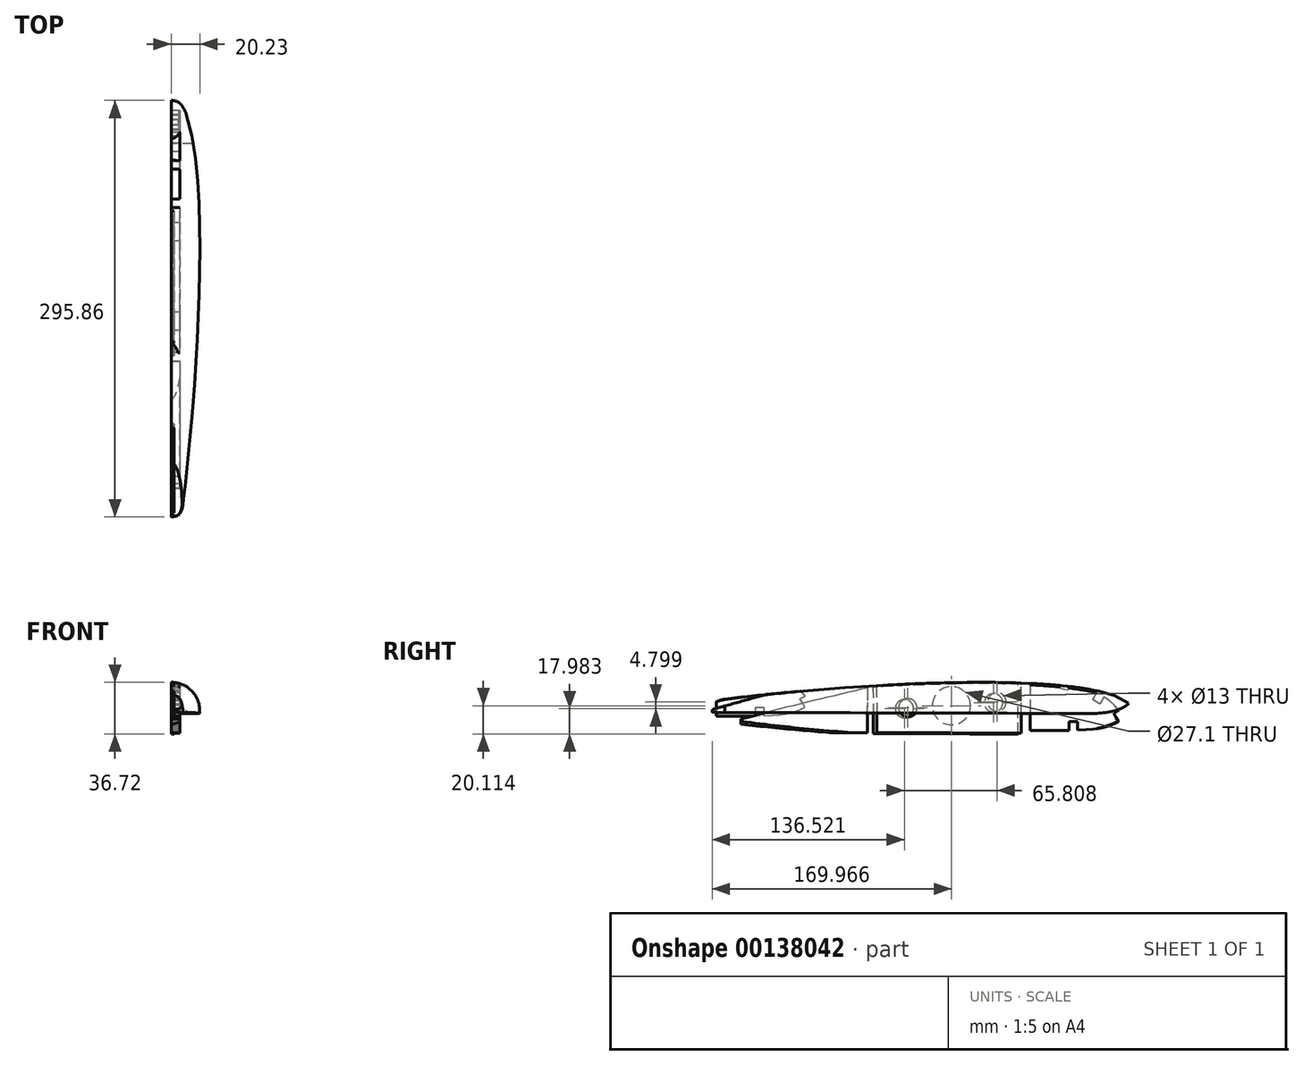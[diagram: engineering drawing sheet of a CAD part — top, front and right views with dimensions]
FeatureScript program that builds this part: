
annotation { "Feature Type Name" : "Feature", "Feature Type Description" : "" }
export const myFeature = defineFeature(function(context is Context, id is Id, definition is map)
    precondition{}
    {
        {
            var Q0;
            Q0=qCreatedBy(makeId("Right.planeOp"),FACE);
            var sketch = newSketch(context, id + "F0", { "sketchPlane" : qUnion([Q0])});
            skLineSegment(sketch, "E0", {"start": v(-158.36, 59.6) * mm, "end": v(-43.4, 59.28) * mm});
            skLineSegment(sketch, "E1", {"start": v(-43.4, 59.28) * mm, "end": v(-43.4, 68.43) * mm});
            skLineSegment(sketch, "E2", {"start": v(-43.4, 68.43) * mm, "end": v(-37.2, 68.43) * mm});
            skLineSegment(sketch, "E3", {"start": v(-37.2, 68.43) * mm, "end": v(-37.2, 59.28) * mm});
            skLineSegment(sketch, "E4", {"start": v(-37.2, 59.28) * mm, "end": v(65.82, 58.98) * mm});
            skLineSegment(sketch, "E5", {"start": v(65.82, 58.98) * mm, "end": v(65.82, 70.28) * mm});
            skLineSegment(sketch, "E6", {"start": v(65.82, 70.28) * mm, "end": v(72.02, 70.28) * mm});
            skLineSegment(sketch, "E7", {"start": v(72.02, 70.28) * mm, "end": v(72.02, 60.73) * mm});
            skLineSegment(sketch, "E8", {"start": v(72.02, 60.73) * mm, "end": v(99.85, 60.81) * mm});
            skLineSegment(sketch, "E9", {"start": v(99.85, 60.81) * mm, "end": v(99.85, 67.06) * mm});
            skLineSegment(sketch, "E10", {"start": v(99.85, 67.06) * mm, "end": v(105.7, 67.06) * mm});
            skLineSegment(sketch, "E11", {"start": v(105.7, 67.06) * mm, "end": v(105.7, 61.14) * mm});
            skLineSegment(sketch, "E12", {"start": v(105.7, 61.14) * mm, "end": v(111.6, 61.4) * mm});
            skLineSegment(sketch, "E13", {"start": v(111.6, 61.4) * mm, "end": v(116.68, 61.82) * mm});
            skLineSegment(sketch, "E14", {"start": v(116.68, 61.82) * mm, "end": v(121.05, 62.42) * mm});
            skLineSegment(sketch, "E15", {"start": v(121.05, 62.42) * mm, "end": v(124.86, 63.23) * mm});
            skLineSegment(sketch, "E16", {"start": v(124.86, 63.23) * mm, "end": v(128.31, 64.27) * mm});
            skLineSegment(sketch, "E17", {"start": v(128.31, 64.27) * mm, "end": v(131.85, 65.67) * mm});
            skLineSegment(sketch, "E18", {"start": v(131.85, 65.67) * mm, "end": v(134.32, 66.87) * mm});
            skLineSegment(sketch, "E19", {"start": v(134.32, 66.87) * mm, "end": v(130.67, 73.42) * mm});
            skLineSegment(sketch, "E20", {"start": v(130.67, 73.42) * mm, "end": v(134.6, 75.6) * mm});
            skLineSegment(sketch, "E21", {"start": v(134.6, 75.6) * mm, "end": v(132.03, 78.53) * mm});
            skLineSegment(sketch, "E22", {"start": v(132.03, 78.53) * mm, "end": v(128.46, 81.7) * mm});
            skLineSegment(sketch, "E23", {"start": v(128.46, 81.7) * mm, "end": v(124.52, 84.4) * mm});
            skLineSegment(sketch, "E24", {"start": v(124.52, 84.4) * mm, "end": v(121.47, 79.12) * mm});
            skLineSegment(sketch, "E25", {"start": v(121.47, 79.12) * mm, "end": v(116.13, 82.2) * mm});
            skLineSegment(sketch, "E26", {"start": v(116.13, 82.2) * mm, "end": v(119.34, 87.78) * mm});
            skLineSegment(sketch, "E27", {"start": v(119.34, 87.78) * mm, "end": v(115.72, 89.55) * mm});
            skLineSegment(sketch, "E28", {"start": v(115.72, 89.55) * mm, "end": v(112.05, 91.25) * mm});
            skLineSegment(sketch, "E29", {"start": v(112.05, 91.25) * mm, "end": v(108.3, 92.8) * mm});
            skLineSegment(sketch, "E30", {"start": v(108.3, 92.8) * mm, "end": v(104.53, 94.12) * mm});
            skLineSegment(sketch, "E31", {"start": v(104.53, 94.12) * mm, "end": v(100.47, 95.16) * mm});
            skLineSegment(sketch, "E32", {"start": v(100.47, 95.16) * mm, "end": v(98.76, 89.3) * mm});
            skLineSegment(sketch, "E33", {"start": v(98.76, 89.3) * mm, "end": v(92.83, 91.04) * mm});
            skLineSegment(sketch, "E34", {"start": v(92.83, 91.04) * mm, "end": v(94.63, 97.2) * mm});
            skLineSegment(sketch, "E35", {"start": v(94.63, 97.2) * mm, "end": v(90.15, 98.07) * mm});
            skLineSegment(sketch, "E36", {"start": v(90.15, 98.07) * mm, "end": v(85.63, 98.85) * mm});
            skLineSegment(sketch, "E37", {"start": v(85.63, 98.85) * mm, "end": v(80.98, 99.54) * mm});
            skLineSegment(sketch, "E38", {"start": v(80.98, 99.54) * mm, "end": v(76.61, 100.13) * mm});
            skLineSegment(sketch, "E39", {"start": v(76.61, 100.13) * mm, "end": v(72.02, 100.6) * mm});
            skLineSegment(sketch, "E40", {"start": v(72.02, 100.6) * mm, "end": v(72.02, 90.28) * mm});
            skLineSegment(sketch, "E41", {"start": v(72.02, 90.28) * mm, "end": v(65.82, 90.28) * mm});
            skLineSegment(sketch, "E42", {"start": v(65.82, 90.28) * mm, "end": v(65.82, 102.3) * mm});
            skLineSegment(sketch, "E43", {"start": v(65.82, 102.3) * mm, "end": v(59.19, 102.27) * mm});
            skLineSegment(sketch, "E44", {"start": v(59.19, 102.27) * mm, "end": v(52.86, 102.17) * mm});
            skLineSegment(sketch, "E45", {"start": v(52.86, 102.17) * mm, "end": v(46.82, 102) * mm});
            skLineSegment(sketch, "E46", {"start": v(46.82, 102) * mm, "end": v(41.06, 101.78) * mm});
            skLineSegment(sketch, "E47", {"start": v(41.06, 101.78) * mm, "end": v(35.53, 101.5) * mm});
            skLineSegment(sketch, "E48", {"start": v(35.53, 101.5) * mm, "end": v(30.24, 101.17) * mm});
            skLineSegment(sketch, "E49", {"start": v(30.24, 101.17) * mm, "end": v(25.14, 100.8) * mm});
            skLineSegment(sketch, "E50", {"start": v(25.14, 100.8) * mm, "end": v(20.23, 100.36) * mm});
            skLineSegment(sketch, "E51", {"start": v(20.23, 100.36) * mm, "end": v(15.48, 99.9) * mm});
            skLineSegment(sketch, "E52", {"start": v(15.48, 99.9) * mm, "end": v(10.86, 99.38) * mm});
            skLineSegment(sketch, "E53", {"start": v(10.86, 99.38) * mm, "end": v(6.36, 98.83) * mm});
            skLineSegment(sketch, "E54", {"start": v(6.36, 98.83) * mm, "end": v(1.95, 98.25) * mm});
            skLineSegment(sketch, "E55", {"start": v(1.95, 98.25) * mm, "end": v(-2.38, 97.64) * mm});
            skLineSegment(sketch, "E56", {"start": v(-2.38, 97.64) * mm, "end": v(-6.67, 97) * mm});
            skLineSegment(sketch, "E57", {"start": v(-6.67, 97) * mm, "end": v(-10.93, 96.35) * mm});
            skLineSegment(sketch, "E58", {"start": v(-10.93, 96.35) * mm, "end": v(-15.18, 95.67) * mm});
            skLineSegment(sketch, "E59", {"start": v(-15.18, 95.67) * mm, "end": v(-19.45, 94.98) * mm});
            skLineSegment(sketch, "E60", {"start": v(-19.45, 94.98) * mm, "end": v(-23.75, 94.27) * mm});
            skLineSegment(sketch, "E61", {"start": v(-23.75, 94.27) * mm, "end": v(-28.12, 93.55) * mm});
            skLineSegment(sketch, "E62", {"start": v(-28.12, 93.55) * mm, "end": v(-32.66, 92.83) * mm});
            skLineSegment(sketch, "E63", {"start": v(-32.66, 92.83) * mm, "end": v(-37.2, 92.1) * mm});
            skLineSegment(sketch, "E64", {"start": v(-37.2, 92.1) * mm, "end": v(-37.2, 81.43) * mm});
            skLineSegment(sketch, "E65", {"start": v(-37.2, 81.43) * mm, "end": v(-43.4, 81.43) * mm});
            skLineSegment(sketch, "E66", {"start": v(-43.4, 81.43) * mm, "end": v(-43.4, 91.03) * mm});
            skLineSegment(sketch, "E67", {"start": v(-43.4, 91.03) * mm, "end": v(-48.14, 89.92) * mm});
            skLineSegment(sketch, "E68", {"start": v(-48.14, 89.92) * mm, "end": v(-52.97, 88.81) * mm});
            skLineSegment(sketch, "E69", {"start": v(-52.97, 88.81) * mm, "end": v(-57.8, 87.7) * mm});
            skLineSegment(sketch, "E70", {"start": v(-57.8, 87.7) * mm, "end": v(-62.63, 86.58) * mm});
            skLineSegment(sketch, "E71", {"start": v(-62.63, 86.58) * mm, "end": v(-67.45, 85.45) * mm});
            skLineSegment(sketch, "E72", {"start": v(-67.45, 85.45) * mm, "end": v(-72.27, 84.3) * mm});
            skLineSegment(sketch, "E73", {"start": v(-72.27, 84.3) * mm, "end": v(-77.1, 83.16) * mm});
            skLineSegment(sketch, "E74", {"start": v(-77.1, 83.16) * mm, "end": v(-81.9, 82) * mm});
            skLineSegment(sketch, "E75", {"start": v(-81.9, 82) * mm, "end": v(-86.72, 80.84) * mm});
            skLineSegment(sketch, "E76", {"start": v(-86.72, 80.84) * mm, "end": v(-91.53, 79.66) * mm});
            skLineSegment(sketch, "E77", {"start": v(-91.53, 79.66) * mm, "end": v(-96.34, 78.48) * mm});
            skLineSegment(sketch, "E78", {"start": v(-96.34, 78.48) * mm, "end": v(-101.14, 77.28) * mm});
            skLineSegment(sketch, "E79", {"start": v(-101.14, 77.28) * mm, "end": v(-105.94, 76.07) * mm});
            skLineSegment(sketch, "E80", {"start": v(-105.94, 76.07) * mm, "end": v(-110.73, 74.85) * mm});
            skLineSegment(sketch, "E81", {"start": v(-110.73, 74.85) * mm, "end": v(-115.52, 73.61) * mm});
            skLineSegment(sketch, "E82", {"start": v(-115.52, 73.61) * mm, "end": v(-120.3, 72.36) * mm});
            skLineSegment(sketch, "E83", {"start": v(-120.3, 72.36) * mm, "end": v(-125.08, 71.1) * mm});
            skLineSegment(sketch, "E84", {"start": v(-125.08, 71.1) * mm, "end": v(-129.85, 69.83) * mm});
            skLineSegment(sketch, "E85", {"start": v(-129.85, 69.83) * mm, "end": v(-134.62, 68.54) * mm});
            skLineSegment(sketch, "E86", {"start": v(-134.62, 68.54) * mm, "end": v(-139.38, 67.23) * mm});
            skLineSegment(sketch, "E87", {"start": v(-139.38, 67.23) * mm, "end": v(-144.14, 65.9) * mm});
            skLineSegment(sketch, "E88", {"start": v(-144.14, 65.9) * mm, "end": v(-148.88, 64.57) * mm});
            skLineSegment(sketch, "E89", {"start": v(-148.88, 64.57) * mm, "end": v(-153.62, 63.21) * mm});
            skLineSegment(sketch, "E90", {"start": v(-153.62, 63.21) * mm, "end": v(-158.36, 61.84) * mm});
            skLineSegment(sketch, "E91", {"start": v(-158.36, 61.84) * mm, "end": v(-158.36, 59.6) * mm});
            skCircle(sketch, "E92", {"center": v(18.63, 79.1) * mm, "radius": 13.55 * mm});
            skPoint(sketch, "E93.end.orphan", {"position": v(5.17, 79.1) * mm});
            skPoint(sketch, "E94.end.orphan", {"position": v(32.08, 79.1) * mm});
            skCircle(sketch, "E95", {"center": v(48.53, 81.13) * mm, "radius": 6.5 * mm});
            skPoint(sketch, "E96.start.orphan", {"position": v(42.17, 81.13) * mm});
            skPoint(sketch, "E97.end.orphan", {"position": v(48.53, 87.5) * mm});
            skCircle(sketch, "E98", {"center": v(-14.82, 76.96) * mm, "radius": 6.5 * mm});
            skPoint(sketch, "E99.end.orphan", {"position": v(-14.82, 83.33) * mm});
            skPoint(sketch, "E100.end.orphan", {"position": v(-21.19, 76.96) * mm});
            skCircle(sketch, "E101", {"center": v(117.36, 70.19) * mm, "radius": 3 * mm});
            skPoint(sketch, "E102.end.orphan", {"position": v(117.36, 73.15) * mm});
            skPoint(sketch, "E103.end.orphan", {"position": v(114.4, 70.19) * mm});
            skCircle(sketch, "E104", {"center": v(-96.87, 68.9) * mm, "radius": 3 * mm});
            skPoint(sketch, "E105.end.orphan", {"position": v(-96.87, 71.86) * mm});
            skPoint(sketch, "E106.end.orphan", {"position": v(-99.84, 68.9) * mm});
            skSolve(sketch);
        }
        {
            var Q0;
            Q0=makeQuery(id+"F0.imprint","IMPRINT",FACE,{"disambiguationData":[TD([[makeQuery(id+"F0.imprint","IMPRINT",EDGE,{"derivedFrom":sQuery(id+"F0.wireOp",EDGE,"E0")}),1.0]])]});
            extrude(context, id + "F1", {"entities" : qUnion([Q0]), "depth" : 6 * mm});
        }
        {
            var Q0;
            Q0=qCreatedBy(makeId("Right.planeOp"),FACE);
            var sketch = newSketch(context, id + "F2", { "sketchPlane" : qUnion([Q0])});
            skLineSegment(sketch, "E107", {"start": v(-44.93, 16.54) * mm, "end": v(-44.6, -16.3) * mm});
            skLineSegment(sketch, "E108", {"start": v(-44.6, -16.3) * mm, "end": v(-39.7, -16.3) * mm});
            skLineSegment(sketch, "E109", {"start": v(-39.7, -16.3) * mm, "end": v(-34.82, -16.32) * mm});
            skLineSegment(sketch, "E110", {"start": v(-34.82, -16.32) * mm, "end": v(-29.94, -16.33) * mm});
            skLineSegment(sketch, "E111", {"start": v(-29.94, -16.33) * mm, "end": v(-25.05, -16.35) * mm});
            skLineSegment(sketch, "E112", {"start": v(-25.05, -16.35) * mm, "end": v(-20.17, -16.36) * mm});
            skLineSegment(sketch, "E113", {"start": v(-20.17, -16.36) * mm, "end": v(-15.28, -16.38) * mm});
            skLineSegment(sketch, "E114", {"start": v(-15.28, -16.38) * mm, "end": v(-10.4, -16.4) * mm});
            skLineSegment(sketch, "E115", {"start": v(-10.4, -16.4) * mm, "end": v(-5.5, -16.4) * mm});
            skLineSegment(sketch, "E116", {"start": v(-5.5, -16.4) * mm, "end": v(-0.62, -16.42) * mm});
            skLineSegment(sketch, "E117", {"start": v(-0.62, -16.42) * mm, "end": v(4.26, -16.43) * mm});
            skLineSegment(sketch, "E118", {"start": v(4.26, -16.43) * mm, "end": v(9.15, -16.45) * mm});
            skLineSegment(sketch, "E119", {"start": v(9.15, -16.45) * mm, "end": v(14.03, -16.46) * mm});
            skLineSegment(sketch, "E120", {"start": v(14.03, -16.46) * mm, "end": v(18.92, -16.48) * mm});
            skLineSegment(sketch, "E121", {"start": v(18.92, -16.48) * mm, "end": v(23.8, -16.5) * mm});
            skLineSegment(sketch, "E122", {"start": v(23.8, -16.5) * mm, "end": v(28.69, -16.5) * mm});
            skLineSegment(sketch, "E123", {"start": v(28.69, -16.5) * mm, "end": v(33.57, -16.52) * mm});
            skLineSegment(sketch, "E124", {"start": v(33.57, -16.52) * mm, "end": v(38.46, -16.53) * mm});
            skLineSegment(sketch, "E125", {"start": v(38.46, -16.53) * mm, "end": v(43.35, -16.55) * mm});
            skLineSegment(sketch, "E126", {"start": v(43.35, -16.55) * mm, "end": v(48.23, -16.56) * mm});
            skLineSegment(sketch, "E127", {"start": v(48.23, -16.56) * mm, "end": v(53.12, -16.58) * mm});
            skLineSegment(sketch, "E128", {"start": v(53.12, -16.58) * mm, "end": v(58, -16.6) * mm});
            skLineSegment(sketch, "E129", {"start": v(58, -16.6) * mm, "end": v(58, 26.73) * mm});
            skLineSegment(sketch, "E130", {"start": v(51.37, 26.7) * mm, "end": v(45.04, 26.6) * mm});
            skLineSegment(sketch, "E131", {"start": v(45.04, 26.6) * mm, "end": v(39, 26.43) * mm});
            skLineSegment(sketch, "E132", {"start": v(39, 26.43) * mm, "end": v(33.23, 26.21) * mm});
            skLineSegment(sketch, "E133", {"start": v(33.23, 26.21) * mm, "end": v(27.71, 25.93) * mm});
            skLineSegment(sketch, "E134", {"start": v(27.71, 25.93) * mm, "end": v(22.42, 25.6) * mm});
            skLineSegment(sketch, "E135", {"start": v(22.42, 25.6) * mm, "end": v(17.32, 25.22) * mm});
            skLineSegment(sketch, "E136", {"start": v(17.32, 25.22) * mm, "end": v(12.4, 24.8) * mm});
            skLineSegment(sketch, "E137", {"start": v(12.4, 24.8) * mm, "end": v(7.65, 24.32) * mm});
            skLineSegment(sketch, "E138", {"start": v(7.65, 24.32) * mm, "end": v(3.04, 23.8) * mm});
            skLineSegment(sketch, "E139", {"start": v(3.04, 23.8) * mm, "end": v(-1.46, 23.26) * mm});
            skLineSegment(sketch, "E140", {"start": v(-1.46, 23.26) * mm, "end": v(-5.87, 22.68) * mm});
            skLineSegment(sketch, "E141", {"start": v(-5.87, 22.68) * mm, "end": v(-10.2, 22.07) * mm});
            skLineSegment(sketch, "E142", {"start": v(-10.2, 22.07) * mm, "end": v(-14.5, 21.44) * mm});
            skLineSegment(sketch, "E143", {"start": v(-14.5, 21.44) * mm, "end": v(-18.75, 20.78) * mm});
            skLineSegment(sketch, "E144", {"start": v(-18.75, 20.78) * mm, "end": v(-23, 20.1) * mm});
            skLineSegment(sketch, "E145", {"start": v(-23, 20.1) * mm, "end": v(-27.27, 19.4) * mm});
            skLineSegment(sketch, "E146", {"start": v(-27.27, 19.4) * mm, "end": v(-31.57, 18.7) * mm});
            skLineSegment(sketch, "E147", {"start": v(-31.57, 18.7) * mm, "end": v(-35.94, 17.98) * mm});
            skLineSegment(sketch, "E148", {"start": v(-35.94, 17.98) * mm, "end": v(-40.38, 17.26) * mm});
            skLineSegment(sketch, "E149", {"start": v(-40.38, 17.26) * mm, "end": v(-44.93, 16.54) * mm});
            skCircle(sketch, "E150", {"center": v(10.8, 3.52) * mm, "radius": 13.55 * mm});
            skCircle(sketch, "E151", {"center": v(40.71, 5.56) * mm, "radius": 6.5 * mm});
            skCircle(sketch, "E152", {"center": v(-22.64, 1.4) * mm, "radius": 6.5 * mm});
            skLineSegment(sketch, "E153", {"start": v(51.37, 26.7) * mm, "end": v(58, 26.73) * mm});
            skLineSegment(sketch, "E154", {"start": v(-271.5, -5.35) * mm, "end": v(-271.4, 26.4) * mm});
            skLineSegment(sketch, "E155", {"start": v(-156.16, 35.97) * mm, "end": v(-156.16, -3.9) * mm});
            skLineSegment(sketch, "E156", {"start": v(-156.16, -3.9) * mm, "end": v(-151.52, -3.88) * mm});
            skLineSegment(sketch, "E157", {"start": v(-151.52, -3.88) * mm, "end": v(-146.89, -3.87) * mm});
            skLineSegment(sketch, "E158", {"start": v(-146.89, -3.87) * mm, "end": v(-142.25, -3.85) * mm});
            skLineSegment(sketch, "E159", {"start": v(-142.25, -3.85) * mm, "end": v(-137.61, -3.84) * mm});
            skLineSegment(sketch, "E160", {"start": v(-137.61, -3.84) * mm, "end": v(-132.97, -3.83) * mm});
            skLineSegment(sketch, "E161", {"start": v(-132.97, -3.83) * mm, "end": v(-128.34, -3.81) * mm});
            skLineSegment(sketch, "E162", {"start": v(-128.34, -3.81) * mm, "end": v(-128.34, -0.7) * mm});
            skLineSegment(sketch, "E163", {"start": v(-128.34, -0.7) * mm, "end": v(-128.34, 2.43) * mm});
            skLineSegment(sketch, "E164", {"start": v(-128.34, 2.43) * mm, "end": v(-125.42, 2.43) * mm});
            skLineSegment(sketch, "E165", {"start": v(-125.42, 2.43) * mm, "end": v(-122.5, 2.43) * mm});
            skLineSegment(sketch, "E166", {"start": v(-122.5, 2.43) * mm, "end": v(-122.5, -0.53) * mm});
            skLineSegment(sketch, "E167", {"start": v(-122.5, -0.53) * mm, "end": v(-122.5, -3.49) * mm});
            skLineSegment(sketch, "E168", {"start": v(-122.5, -3.49) * mm, "end": v(-116.5, -3.23) * mm});
            skLineSegment(sketch, "E169", {"start": v(-116.5, -3.23) * mm, "end": v(-111.4, -2.8) * mm});
            skLineSegment(sketch, "E170", {"start": v(-111.4, -2.8) * mm, "end": v(-107.04, -2.2) * mm});
            skLineSegment(sketch, "E171", {"start": v(-107.04, -2.2) * mm, "end": v(-103.22, -1.4) * mm});
            skLineSegment(sketch, "E172", {"start": v(-103.22, -1.4) * mm, "end": v(-99.77, -0.36) * mm});
            skLineSegment(sketch, "E173", {"start": v(-99.77, -0.36) * mm, "end": v(-96.52, 0.94) * mm});
            skLineSegment(sketch, "E174", {"start": v(-96.52, 0.94) * mm, "end": v(-93.27, 2.52) * mm});
            skLineSegment(sketch, "E175", {"start": v(-93.27, 2.52) * mm, "end": v(-94.98, 5.5) * mm});
            skLineSegment(sketch, "E176", {"start": v(-94.98, 5.5) * mm, "end": v(-96.69, 8.47) * mm});
            skLineSegment(sketch, "E177", {"start": v(-96.69, 8.47) * mm, "end": v(-93.06, 10.5) * mm});
            skLineSegment(sketch, "E178", {"start": v(-93.06, 10.5) * mm, "end": v(-96.06, 13.9) * mm});
            skLineSegment(sketch, "E179", {"start": v(-96.06, 13.9) * mm, "end": v(-99.62, 17.07) * mm});
            skLineSegment(sketch, "E180", {"start": v(-99.62, 17.07) * mm, "end": v(-103.65, 20.07) * mm});
            skLineSegment(sketch, "E181", {"start": v(-103.65, 20.07) * mm, "end": v(-105.04, 17.44) * mm});
            skLineSegment(sketch, "E182", {"start": v(-105.04, 17.44) * mm, "end": v(-106.43, 14.82) * mm});
            skLineSegment(sketch, "E183", {"start": v(-106.43, 14.82) * mm, "end": v(-109.05, 16.44) * mm});
            skLineSegment(sketch, "E184", {"start": v(-109.05, 16.44) * mm, "end": v(-111.68, 18.06) * mm});
            skLineSegment(sketch, "E185", {"start": v(-111.68, 18.06) * mm, "end": v(-110.21, 20.6) * mm});
            skLineSegment(sketch, "E186", {"start": v(-110.21, 20.6) * mm, "end": v(-108.74, 23.16) * mm});
            skLineSegment(sketch, "E187", {"start": v(-108.74, 23.16) * mm, "end": v(-112.37, 24.92) * mm});
            skLineSegment(sketch, "E188", {"start": v(-112.37, 24.92) * mm, "end": v(-116.04, 26.62) * mm});
            skLineSegment(sketch, "E189", {"start": v(-116.04, 26.62) * mm, "end": v(-119.8, 28.18) * mm});
            skLineSegment(sketch, "E190", {"start": v(-119.8, 28.18) * mm, "end": v(-123.68, 29.52) * mm});
            skLineSegment(sketch, "E191", {"start": v(-123.68, 29.52) * mm, "end": v(-127.74, 30.57) * mm});
            skLineSegment(sketch, "E192", {"start": v(-127.74, 30.57) * mm, "end": v(-128.5, 27.71) * mm});
            skLineSegment(sketch, "E193", {"start": v(-128.5, 27.71) * mm, "end": v(-129.28, 24.85) * mm});
            skLineSegment(sketch, "E194", {"start": v(-129.28, 24.85) * mm, "end": v(-132.3, 25.55) * mm});
            skLineSegment(sketch, "E195", {"start": v(-132.3, 25.55) * mm, "end": v(-135.3, 26.24) * mm});
            skLineSegment(sketch, "E196", {"start": v(-135.3, 26.24) * mm, "end": v(-134.38, 29.4) * mm});
            skLineSegment(sketch, "E197", {"start": v(-134.38, 29.4) * mm, "end": v(-133.45, 32.58) * mm});
            skLineSegment(sketch, "E198", {"start": v(-133.45, 32.58) * mm, "end": v(-137.94, 33.44) * mm});
            skLineSegment(sketch, "E199", {"start": v(-137.94, 33.44) * mm, "end": v(-142.46, 34.22) * mm});
            skLineSegment(sketch, "E200", {"start": v(-142.46, 34.22) * mm, "end": v(-147, 34.91) * mm});
            skLineSegment(sketch, "E201", {"start": v(-147, 34.91) * mm, "end": v(-151.57, 35.5) * mm});
            skLineSegment(sketch, "E202", {"start": v(-151.57, 35.5) * mm, "end": v(-156.16, 35.97) * mm});
            skLineSegment(sketch, "E203", {"start": v(-271.4, 26.4) * mm, "end": v(-276.23, 25.3) * mm});
            skLineSegment(sketch, "E204", {"start": v(-276.23, 25.3) * mm, "end": v(-281.06, 24.19) * mm});
            skLineSegment(sketch, "E205", {"start": v(-281.06, 24.19) * mm, "end": v(-285.89, 23.07) * mm});
            skLineSegment(sketch, "E206", {"start": v(-285.89, 23.07) * mm, "end": v(-290.71, 21.95) * mm});
            skLineSegment(sketch, "E207", {"start": v(-290.71, 21.95) * mm, "end": v(-295.54, 20.82) * mm});
            skLineSegment(sketch, "E208", {"start": v(-295.54, 20.82) * mm, "end": v(-300.36, 19.68) * mm});
            skLineSegment(sketch, "E209", {"start": v(-300.36, 19.68) * mm, "end": v(-305.18, 18.53) * mm});
            skLineSegment(sketch, "E210", {"start": v(-305.18, 18.53) * mm, "end": v(-310, 17.38) * mm});
            skLineSegment(sketch, "E211", {"start": v(-310, 17.38) * mm, "end": v(-314.8, 16.21) * mm});
            skLineSegment(sketch, "E212", {"start": v(-314.8, 16.21) * mm, "end": v(-319.62, 15.03) * mm});
            skLineSegment(sketch, "E213", {"start": v(-319.62, 15.03) * mm, "end": v(-324.43, 13.85) * mm});
            skLineSegment(sketch, "E214", {"start": v(-324.43, 13.85) * mm, "end": v(-329.23, 12.65) * mm});
            skLineSegment(sketch, "E215", {"start": v(-329.23, 12.65) * mm, "end": v(-334.03, 11.44) * mm});
            skLineSegment(sketch, "E216", {"start": v(-334.03, 11.44) * mm, "end": v(-338.82, 10.22) * mm});
            skLineSegment(sketch, "E217", {"start": v(-338.82, 10.22) * mm, "end": v(-343.6, 8.98) * mm});
            skLineSegment(sketch, "E218", {"start": v(-343.6, 8.98) * mm, "end": v(-348.4, 7.74) * mm});
            skLineSegment(sketch, "E219", {"start": v(-348.4, 7.74) * mm, "end": v(-353.17, 6.47) * mm});
            skLineSegment(sketch, "E220", {"start": v(-353.17, 6.47) * mm, "end": v(-357.94, 5.2) * mm});
            skLineSegment(sketch, "E221", {"start": v(-271.5, -5.35) * mm, "end": v(-361.14, -5.08) * mm});
            skLineSegment(sketch, "E222", {"start": v(-361.14, -5.08) * mm, "end": v(-361.14, 4.33) * mm});
            skLineSegment(sketch, "E223", {"start": v(-361.14, 4.33) * mm, "end": v(-357.94, 5.2) * mm});
            skSolve(sketch);
        }
        {
            var Q0;
            Q0=qCreatedBy(makeId("Right.planeOp"),FACE);
            var sketch = newSketch(context, id + "F3", { "sketchPlane" : qUnion([Q0])});
            skLineSegment(sketch, "E224", {"start": v(-48.77, -15.66) * mm, "end": v(-48.68, 16.08) * mm});
            skLineSegment(sketch, "E225", {"start": v(-42.47, 17.17) * mm, "end": v(-42.14, -15.66) * mm});
            skLineSegment(sketch, "E226", {"start": v(-42.14, -15.66) * mm, "end": v(-37.25, -15.68) * mm});
            skLineSegment(sketch, "E227", {"start": v(-37.25, -15.68) * mm, "end": v(-32.36, -15.7) * mm});
            skLineSegment(sketch, "E228", {"start": v(-32.36, -15.7) * mm, "end": v(-27.48, -15.7) * mm});
            skLineSegment(sketch, "E229", {"start": v(-27.48, -15.7) * mm, "end": v(-22.6, -15.72) * mm});
            skLineSegment(sketch, "E230", {"start": v(-22.6, -15.72) * mm, "end": v(-17.7, -15.73) * mm});
            skLineSegment(sketch, "E231", {"start": v(-17.7, -15.73) * mm, "end": v(-12.82, -15.75) * mm});
            skLineSegment(sketch, "E232", {"start": v(-12.82, -15.75) * mm, "end": v(-7.94, -15.76) * mm});
            skLineSegment(sketch, "E233", {"start": v(-7.94, -15.76) * mm, "end": v(-3.05, -15.78) * mm});
            skLineSegment(sketch, "E234", {"start": v(-3.05, -15.78) * mm, "end": v(1.83, -15.8) * mm});
            skLineSegment(sketch, "E235", {"start": v(1.83, -15.8) * mm, "end": v(6.72, -15.8) * mm});
            skLineSegment(sketch, "E236", {"start": v(6.72, -15.8) * mm, "end": v(11.6, -15.82) * mm});
            skLineSegment(sketch, "E237", {"start": v(11.6, -15.82) * mm, "end": v(16.5, -15.83) * mm});
            skLineSegment(sketch, "E238", {"start": v(16.5, -15.83) * mm, "end": v(21.38, -15.85) * mm});
            skLineSegment(sketch, "E239", {"start": v(21.38, -15.85) * mm, "end": v(26.26, -15.86) * mm});
            skLineSegment(sketch, "E240", {"start": v(26.26, -15.86) * mm, "end": v(31.15, -15.88) * mm});
            skLineSegment(sketch, "E241", {"start": v(31.15, -15.88) * mm, "end": v(36.03, -15.9) * mm});
            skLineSegment(sketch, "E242", {"start": v(36.03, -15.9) * mm, "end": v(40.92, -15.9) * mm});
            skLineSegment(sketch, "E243", {"start": v(40.92, -15.9) * mm, "end": v(45.8, -15.92) * mm});
            skLineSegment(sketch, "E244", {"start": v(45.8, -15.92) * mm, "end": v(50.69, -15.93) * mm});
            skLineSegment(sketch, "E245", {"start": v(50.69, -15.93) * mm, "end": v(55.57, -15.95) * mm});
            skLineSegment(sketch, "E246", {"start": v(55.57, -15.95) * mm, "end": v(60.46, -15.96) * mm});
            skLineSegment(sketch, "E247", {"start": v(60.46, -15.96) * mm, "end": v(60.46, 27.36) * mm});
            skLineSegment(sketch, "E248", {"start": v(66.56, 25.66) * mm, "end": v(66.56, -14.2) * mm});
            skLineSegment(sketch, "E249", {"start": v(66.56, -14.2) * mm, "end": v(71.2, -14.2) * mm});
            skLineSegment(sketch, "E250", {"start": v(71.2, -14.2) * mm, "end": v(75.84, -14.18) * mm});
            skLineSegment(sketch, "E251", {"start": v(75.84, -14.18) * mm, "end": v(80.47, -14.17) * mm});
            skLineSegment(sketch, "E252", {"start": v(80.47, -14.17) * mm, "end": v(85.11, -14.15) * mm});
            skLineSegment(sketch, "E253", {"start": v(85.11, -14.15) * mm, "end": v(89.75, -14.14) * mm});
            skLineSegment(sketch, "E254", {"start": v(89.75, -14.14) * mm, "end": v(94.39, -14.13) * mm});
            skLineSegment(sketch, "E255", {"start": v(94.39, -14.13) * mm, "end": v(94.39, -11) * mm});
            skLineSegment(sketch, "E256", {"start": v(94.39, -11) * mm, "end": v(94.39, -7.88) * mm});
            skLineSegment(sketch, "E257", {"start": v(94.39, -7.88) * mm, "end": v(97.3, -7.88) * mm});
            skLineSegment(sketch, "E258", {"start": v(97.3, -7.88) * mm, "end": v(100.23, -7.88) * mm});
            skLineSegment(sketch, "E259", {"start": v(100.23, -7.88) * mm, "end": v(100.23, -10.84) * mm});
            skLineSegment(sketch, "E260", {"start": v(100.23, -10.84) * mm, "end": v(100.23, -13.8) * mm});
            skLineSegment(sketch, "E261", {"start": v(100.23, -13.8) * mm, "end": v(106.23, -13.54) * mm});
            skLineSegment(sketch, "E262", {"start": v(106.23, -13.54) * mm, "end": v(111.32, -13.12) * mm});
            skLineSegment(sketch, "E263", {"start": v(111.32, -13.12) * mm, "end": v(115.68, -12.52) * mm});
            skLineSegment(sketch, "E264", {"start": v(115.68, -12.52) * mm, "end": v(119.5, -11.71) * mm});
            skLineSegment(sketch, "E265", {"start": v(119.5, -11.71) * mm, "end": v(122.95, -10.67) * mm});
            skLineSegment(sketch, "E266", {"start": v(122.95, -10.67) * mm, "end": v(126.2, -9.37) * mm});
            skLineSegment(sketch, "E267", {"start": v(126.2, -9.37) * mm, "end": v(129.46, -7.8) * mm});
            skLineSegment(sketch, "E268", {"start": v(129.46, -7.8) * mm, "end": v(127.75, -4.82) * mm});
            skLineSegment(sketch, "E269", {"start": v(127.75, -4.82) * mm, "end": v(126.03, -1.85) * mm});
            skLineSegment(sketch, "E270", {"start": v(126.03, -1.85) * mm, "end": v(129.66, 0.18) * mm});
            skLineSegment(sketch, "E271", {"start": v(129.66, 0.18) * mm, "end": v(126.66, 3.58) * mm});
            skLineSegment(sketch, "E272", {"start": v(126.66, 3.58) * mm, "end": v(123.1, 6.76) * mm});
            skLineSegment(sketch, "E273", {"start": v(123.1, 6.76) * mm, "end": v(119.08, 9.75) * mm});
            skLineSegment(sketch, "E274", {"start": v(119.08, 9.75) * mm, "end": v(117.69, 7.13) * mm});
            skLineSegment(sketch, "E275", {"start": v(117.69, 7.13) * mm, "end": v(116.3, 4.5) * mm});
            skLineSegment(sketch, "E276", {"start": v(116.3, 4.5) * mm, "end": v(113.67, 6.13) * mm});
            skLineSegment(sketch, "E277", {"start": v(113.67, 6.13) * mm, "end": v(111.05, 7.75) * mm});
            skLineSegment(sketch, "E278", {"start": v(111.05, 7.75) * mm, "end": v(112.51, 10.3) * mm});
            skLineSegment(sketch, "E279", {"start": v(112.51, 10.3) * mm, "end": v(113.98, 12.84) * mm});
            skLineSegment(sketch, "E280", {"start": v(113.98, 12.84) * mm, "end": v(110.35, 14.61) * mm});
            skLineSegment(sketch, "E281", {"start": v(110.35, 14.61) * mm, "end": v(106.68, 16.31) * mm});
            skLineSegment(sketch, "E282", {"start": v(106.68, 16.31) * mm, "end": v(102.93, 17.87) * mm});
            skLineSegment(sketch, "E283", {"start": v(102.93, 17.87) * mm, "end": v(99.05, 19.2) * mm});
            skLineSegment(sketch, "E284", {"start": v(99.05, 19.2) * mm, "end": v(94.99, 20.25) * mm});
            skLineSegment(sketch, "E285", {"start": v(94.99, 20.25) * mm, "end": v(94.21, 17.4) * mm});
            skLineSegment(sketch, "E286", {"start": v(94.21, 17.4) * mm, "end": v(93.44, 14.54) * mm});
            skLineSegment(sketch, "E287", {"start": v(93.44, 14.54) * mm, "end": v(90.43, 15.24) * mm});
            skLineSegment(sketch, "E288", {"start": v(90.43, 15.24) * mm, "end": v(87.42, 15.93) * mm});
            skLineSegment(sketch, "E289", {"start": v(87.42, 15.93) * mm, "end": v(88.35, 19.1) * mm});
            skLineSegment(sketch, "E290", {"start": v(88.35, 19.1) * mm, "end": v(89.27, 22.26) * mm});
            skLineSegment(sketch, "E291", {"start": v(89.27, 22.26) * mm, "end": v(84.78, 23.13) * mm});
            skLineSegment(sketch, "E292", {"start": v(84.78, 23.13) * mm, "end": v(80.26, 23.91) * mm});
            skLineSegment(sketch, "E293", {"start": v(80.26, 23.91) * mm, "end": v(75.72, 24.6) * mm});
            skLineSegment(sketch, "E294", {"start": v(75.72, 24.6) * mm, "end": v(71.15, 25.19) * mm});
            skLineSegment(sketch, "E295", {"start": v(71.15, 25.19) * mm, "end": v(66.56, 25.66) * mm});
            skLineSegment(sketch, "E296", {"start": v(60.46, 27.36) * mm, "end": v(53.82, 27.32) * mm});
            skLineSegment(sketch, "E297", {"start": v(53.82, 27.32) * mm, "end": v(47.5, 27.23) * mm});
            skLineSegment(sketch, "E298", {"start": v(47.5, 27.23) * mm, "end": v(41.46, 27.06) * mm});
            skLineSegment(sketch, "E299", {"start": v(41.46, 27.06) * mm, "end": v(35.7, 26.84) * mm});
            skLineSegment(sketch, "E300", {"start": v(35.7, 26.84) * mm, "end": v(30.17, 26.56) * mm});
            skLineSegment(sketch, "E301", {"start": v(30.17, 26.56) * mm, "end": v(24.87, 26.23) * mm});
            skLineSegment(sketch, "E302", {"start": v(24.87, 26.23) * mm, "end": v(19.78, 25.85) * mm});
            skLineSegment(sketch, "E303", {"start": v(19.78, 25.85) * mm, "end": v(14.87, 25.42) * mm});
            skLineSegment(sketch, "E304", {"start": v(14.87, 25.42) * mm, "end": v(10.11, 24.95) * mm});
            skLineSegment(sketch, "E305", {"start": v(10.11, 24.95) * mm, "end": v(5.5, 24.44) * mm});
            skLineSegment(sketch, "E306", {"start": v(5.5, 24.44) * mm, "end": v(1, 23.9) * mm});
            skLineSegment(sketch, "E307", {"start": v(1, 23.9) * mm, "end": v(-3.41, 23.31) * mm});
            skLineSegment(sketch, "E308", {"start": v(-3.41, 23.31) * mm, "end": v(-7.75, 22.7) * mm});
            skLineSegment(sketch, "E309", {"start": v(-7.75, 22.7) * mm, "end": v(-12.03, 22.07) * mm});
            skLineSegment(sketch, "E310", {"start": v(-12.03, 22.07) * mm, "end": v(-16.3, 21.4) * mm});
            skLineSegment(sketch, "E311", {"start": v(-16.3, 21.4) * mm, "end": v(-20.54, 20.73) * mm});
            skLineSegment(sketch, "E312", {"start": v(-20.54, 20.73) * mm, "end": v(-24.81, 20.04) * mm});
            skLineSegment(sketch, "E313", {"start": v(-24.81, 20.04) * mm, "end": v(-29.12, 19.33) * mm});
            skLineSegment(sketch, "E314", {"start": v(-29.12, 19.33) * mm, "end": v(-33.48, 18.61) * mm});
            skLineSegment(sketch, "E315", {"start": v(-33.48, 18.61) * mm, "end": v(-37.92, 17.9) * mm});
            skLineSegment(sketch, "E316", {"start": v(-37.92, 17.9) * mm, "end": v(-42.47, 17.17) * mm});
            skLineSegment(sketch, "E317", {"start": v(-48.68, 16.08) * mm, "end": v(-53.5, 14.98) * mm});
            skLineSegment(sketch, "E318", {"start": v(-53.5, 14.98) * mm, "end": v(-58.34, 13.87) * mm});
            skLineSegment(sketch, "E319", {"start": v(-58.34, 13.87) * mm, "end": v(-63.16, 12.76) * mm});
            skLineSegment(sketch, "E320", {"start": v(-63.16, 12.76) * mm, "end": v(-68, 11.63) * mm});
            skLineSegment(sketch, "E321", {"start": v(-68, 11.63) * mm, "end": v(-72.82, 10.5) * mm});
            skLineSegment(sketch, "E322", {"start": v(-72.82, 10.5) * mm, "end": v(-77.64, 9.37) * mm});
            skLineSegment(sketch, "E323", {"start": v(-77.64, 9.37) * mm, "end": v(-82.46, 8.22) * mm});
            skLineSegment(sketch, "E324", {"start": v(-82.46, 8.22) * mm, "end": v(-87.27, 7.06) * mm});
            skLineSegment(sketch, "E325", {"start": v(-87.27, 7.06) * mm, "end": v(-92.09, 5.9) * mm});
            skLineSegment(sketch, "E326", {"start": v(-92.09, 5.9) * mm, "end": v(-96.9, 4.72) * mm});
            skLineSegment(sketch, "E327", {"start": v(-96.9, 4.72) * mm, "end": v(-101.7, 3.53) * mm});
            skLineSegment(sketch, "E328", {"start": v(-101.7, 3.53) * mm, "end": v(-106.5, 2.34) * mm});
            skLineSegment(sketch, "E329", {"start": v(-106.5, 2.34) * mm, "end": v(-111.3, 1.13) * mm});
            skLineSegment(sketch, "E330", {"start": v(-111.3, 1.13) * mm, "end": v(-116.1, -0.1) * mm});
            skLineSegment(sketch, "E331", {"start": v(-116.1, -0.1) * mm, "end": v(-120.88, -1.33) * mm});
            skLineSegment(sketch, "E332", {"start": v(-120.88, -1.33) * mm, "end": v(-125.67, -2.58) * mm});
            skLineSegment(sketch, "E333", {"start": v(-125.67, -2.58) * mm, "end": v(-130.45, -3.84) * mm});
            skLineSegment(sketch, "E334", {"start": v(-130.45, -3.84) * mm, "end": v(-135.58, -5.12) * mm});
            skCircle(sketch, "E335", {"center": v(43.17, 6.2) * mm, "radius": 6.5 * mm});
            skCircle(sketch, "E336", {"center": v(-20.18, 2.02) * mm, "radius": 6.5 * mm});
            skLineSegment(sketch, "E337", {"start": v(-48.77, -15.66) * mm, "end": v(-138.77, -15.4) * mm});
            skLineSegment(sketch, "E338", {"start": v(-138.77, -15.4) * mm, "end": v(-138.77, -5.98) * mm});
            skLineSegment(sketch, "E339", {"start": v(-138.77, -5.98) * mm, "end": v(-135.58, -5.12) * mm});
            skSolve(sketch);
        }
        {
            var Q0;
            Q0=makeQuery(id+"F3.imprint","IMPRINT",FACE,{"disambiguationData":[TD([[makeQuery(id+"F3.imprint","IMPRINT",EDGE,{"derivedFrom":sQuery(id+"F3.wireOp",EDGE,"E248")}),1.0]])]});
            var Q1;
            Q1=makeQuery(id+"F3.imprint","IMPRINT",FACE,{"disambiguationData":[TD([[makeQuery(id+"F3.imprint","IMPRINT",EDGE,{"derivedFrom":sQuery(id+"F3.wireOp",EDGE,"25496b68-b062-417b-a34f-ccdf0e89dc9b")}),1.0]])]});
            var Q2;
            Q2=makeQuery(id+"F3.imprint","IMPRINT",FACE,{"disambiguationData":[TD([[makeQuery(id+"F3.imprint","IMPRINT",EDGE,{"derivedFrom":sQuery(id+"F3.wireOp",EDGE,"E225")}),1.0]])]});
            var Q3;
            Q3=makeQuery(id+"F3.imprint","IMPRINT",FACE,{"disambiguationData":[TD([[makeQuery(id+"F3.imprint","IMPRINT",EDGE,{"derivedFrom":sQuery(id+"F3.wireOp",EDGE,"E224")}),1.0]])]});
            extrude(context, id + "F4", {"entities" : qUnion([Q0, Q1, Q2, Q3]), "depth" : 6 * mm});
        }
        {
            var Q0;
            Q0=makeQuery(id+"F2.imprint","IMPRINT",FACE,{"disambiguationData":[TD([[makeQuery(id+"F2.imprint","IMPRINT",EDGE,{"derivedFrom":sQuery(id+"F2.wireOp",EDGE,"E107")}),1.0]])]});
            var Q1;
            Q1=makeQuery(id+"F2.imprint","IMPRINT",FACE,{"disambiguationData":[TD([[makeQuery(id+"F2.imprint","IMPRINT",EDGE,{"derivedFrom":sQuery(id+"F2.wireOp",EDGE,"E154")}),1.0]])]});
            var Q2;
            Q2=makeQuery(id+"F2.imprint","IMPRINT",FACE,{"disambiguationData":[TD([[makeQuery(id+"F2.imprint","IMPRINT",EDGE,{"derivedFrom":sQuery(id+"F2.wireOp",EDGE,"E155")}),1.0]])]});
            var Q3;
            Q3=sQuery(id+"F2.wireOp",EDGE,"E127");
            var Q4;
            Q4=sQuery(id+"F2.wireOp",EDGE,"E119");
            var Q5;
            Q5=sQuery(id+"F2.wireOp",EDGE,"E111");
            var Q6;
            Q6=sQuery(id+"F2.wireOp",EDGE,"E107");
            var Q7;
            Q7=sQuery(id+"F2.wireOp",EDGE,"E122");
            var Q8;
            Q8=sQuery(id+"F2.wireOp",EDGE,"E144");
            var Q9;
            Q9=sQuery(id+"F2.wireOp",EDGE,"E109");
            var Q10;
            Q10=sQuery(id+"F2.wireOp",EDGE,"E128");
            var Q11;
            Q11=sQuery(id+"F2.wireOp",EDGE,"E114");
            var Q12;
            Q12=sQuery(id+"F2.wireOp",EDGE,"E140");
            var Q13;
            Q13=sQuery(id+"F2.wireOp",EDGE,"E145");
            var Q14;
            Q14=sQuery(id+"F2.wireOp",EDGE,"E149");
            var Q15;
            Q15=sQuery(id+"F2.wireOp",EDGE,"E121");
            var Q16;
            Q16=sQuery(id+"F2.wireOp",EDGE,"E116");
            var Q17;
            Q17=sQuery(id+"F2.wireOp",EDGE,"E138");
            var Q18;
            Q18=sQuery(id+"F2.wireOp",EDGE,"E146");
            var Q19;
            Q19=sQuery(id+"F2.wireOp",EDGE,"E123");
            var Q20;
            Q20=sQuery(id+"F2.wireOp",EDGE,"E142");
            var Q21;
            Q21=sQuery(id+"F2.wireOp",EDGE,"E126");
            var Q22;
            Q22=sQuery(id+"F2.wireOp",EDGE,"E147");
            var Q23;
            Q23=sQuery(id+"F2.wireOp",EDGE,"E141");
            var Q24;
            Q24=sQuery(id+"F2.wireOp",EDGE,"E135");
            var Q25;
            Q25=sQuery(id+"F2.wireOp",EDGE,"E125");
            var Q26;
            Q26=sQuery(id+"F2.wireOp",EDGE,"E124");
            var Q27;
            Q27=sQuery(id+"F2.wireOp",EDGE,"E108");
            var Q28;
            Q28=sQuery(id+"F2.wireOp",EDGE,"E136");
            var Q29;
            Q29=sQuery(id+"F2.wireOp",EDGE,"E137");
            var Q30;
            Q30=sQuery(id+"F2.wireOp",EDGE,"E112");
            var Q31;
            Q31=sQuery(id+"F2.wireOp",EDGE,"E113");
            var Q32;
            Q32=sQuery(id+"F2.wireOp",EDGE,"E120");
            var Q33;
            Q33=sQuery(id+"F2.wireOp",EDGE,"E131");
            var Q34;
            Q34=sQuery(id+"F2.wireOp",EDGE,"E143");
            var Q35;
            Q35=sQuery(id+"F2.wireOp",EDGE,"E133");
            var Q36;
            Q36=sQuery(id+"F2.wireOp",EDGE,"E110");
            var Q37;
            Q37=sQuery(id+"F2.wireOp",EDGE,"E134");
            var Q38;
            Q38=sQuery(id+"F2.wireOp",EDGE,"E115");
            var Q39;
            Q39=sQuery(id+"F2.wireOp",EDGE,"E117");
            var Q40;
            Q40=sQuery(id+"F2.wireOp",EDGE,"E118");
            var Q41;
            Q41=sQuery(id+"F2.wireOp",EDGE,"E139");
            var Q42;
            Q42=sQuery(id+"F2.wireOp",EDGE,"E148");
            var Q43;
            Q43=sQuery(id+"F2.wireOp",EDGE,"E129");
            var Q44;
            Q44=sQuery(id+"F2.wireOp",EDGE,"E130");
            var Q45;
            Q45=sQuery(id+"F2.wireOp",EDGE,"d0833c12-8d8e-4f57-a90d-0691d6c7ca50");
            var Q46;
            Q46=sQuery(id+"F2.wireOp",EDGE,"E132");
            extrude(context, id + "F5", {"entities" : qUnion([Q0, Q1, Q2]), "surfaceEntities" : qUnion([Q3, Q4, Q5, Q6, Q7, Q8, Q9, Q10, Q11, Q12, Q13, Q14, Q15, Q16, Q17, Q18, Q19, Q20, Q21, Q22, Q23, Q24, Q25, Q26, Q27, Q28, Q29, Q30, Q31, Q32, Q33, Q34, Q35, Q36, Q37, Q38, Q39, Q40, Q41, Q42, Q43, Q44, Q45, Q46]), "depth" : 2 * mm});
        }
        {
            var Q0;
            Q0=qCreatedBy(makeId("Right.planeOp"),FACE);
            var sketch = newSketch(context, id + "F6", { "sketchPlane" : qUnion([Q0])});
            skLineSegment(sketch, "E340", {"start": v(-294.95, -36.37) * mm, "end": v(-285.59, -36.37) * mm});
            skLineSegment(sketch, "E341", {"start": v(-285.59, -36.37) * mm, "end": v(-285.59, -42.5) * mm});
            skLineSegment(sketch, "E342", {"start": v(-285.59, -42.5) * mm, "end": v(-265.39, -42.5) * mm});
            skLineSegment(sketch, "E343", {"start": v(-265.39, -42.5) * mm, "end": v(-265.39, -36.4) * mm});
            skLineSegment(sketch, "E344", {"start": v(-265.39, -36.4) * mm, "end": v(-255.95, -36.4) * mm});
            skLineSegment(sketch, "E345", {"start": v(-255.95, -36.4) * mm, "end": v(-255.95, -239.64) * mm});
            skLineSegment(sketch, "E346", {"start": v(-255.95, -239.64) * mm, "end": v(-250.35, -279.52) * mm});
            skLineSegment(sketch, "E347", {"start": v(-250.35, -279.52) * mm, "end": v(-256.39, -280.37) * mm});
            skLineSegment(sketch, "E348", {"start": v(-256.39, -280.37) * mm, "end": v(-249.57, -328.9) * mm});
            skLineSegment(sketch, "E349", {"start": v(-249.57, -328.9) * mm, "end": v(-276.1, -332.62) * mm});
            skLineSegment(sketch, "E350", {"start": v(-276.1, -332.62) * mm, "end": v(-282.93, -284.1) * mm});
            skLineSegment(sketch, "E351", {"start": v(-282.93, -284.1) * mm, "end": v(-288.97, -284.95) * mm});
            skLineSegment(sketch, "E352", {"start": v(-288.97, -284.95) * mm, "end": v(-294.95, -242.37) * mm});
            skLineSegment(sketch, "E353", {"start": v(-294.95, -242.37) * mm, "end": v(-294.95, -36.37) * mm});
            skLineSegment(sketch, "E354", {"start": v(-283.55, -209.17) * mm, "end": v(-267.35, -209.17) * mm});
            skLineSegment(sketch, "E355", {"start": v(-267.35, -209.17) * mm, "end": v(-267.35, -215.37) * mm});
            skLineSegment(sketch, "E356", {"start": v(-267.35, -215.37) * mm, "end": v(-283.55, -215.37) * mm});
            skLineSegment(sketch, "E357", {"start": v(-283.55, -215.37) * mm, "end": v(-283.55, -209.17) * mm});
            skSolve(sketch);
        }
        {
            var Q0;
            Q0=makeQuery(id+"F6.imprint","IMPRINT",FACE,{"disambiguationData":[TD([[makeQuery(id+"F6.imprint","IMPRINT",EDGE,{"derivedFrom":sQuery(id+"F6.wireOp",EDGE,"E340")}),-1.0]])]});
            extrude(context, id + "F7", {"entities" : qUnion([Q0]), "depth" : 6 * mm});
        }
        {
            var Q0;
            Q0=qCreatedBy(makeId("Right.planeOp"),FACE);
            var sketch = newSketch(context, id + "F8", { "sketchPlane" : qUnion([Q0])});
            skLineSegment(sketch, "E358", {"start": v(-222.05, -58.35) * mm, "end": v(-214.56, -58.35) * mm});
            skLineSegment(sketch, "E359", {"start": v(-214.56, -58.35) * mm, "end": v(-214.56, -64.45) * mm});
            skLineSegment(sketch, "E360", {"start": v(-214.56, -64.45) * mm, "end": v(-201.36, -64.45) * mm});
            skLineSegment(sketch, "E361", {"start": v(-201.36, -64.45) * mm, "end": v(-201.36, -58.35) * mm});
            skLineSegment(sketch, "E362", {"start": v(-201.36, -58.35) * mm, "end": v(-193.55, -58.35) * mm});
            skLineSegment(sketch, "E363", {"start": v(-193.55, -58.35) * mm, "end": v(-193.55, -264.35) * mm});
            skLineSegment(sketch, "E364", {"start": v(-193.55, -264.35) * mm, "end": v(-188.2, -302.45) * mm});
            skLineSegment(sketch, "E365", {"start": v(-188.2, -302.45) * mm, "end": v(-194.24, -303.3) * mm});
            skLineSegment(sketch, "E366", {"start": v(-194.24, -303.3) * mm, "end": v(-187.34, -352.38) * mm});
            skLineSegment(sketch, "E367", {"start": v(-187.34, -352.38) * mm, "end": v(-203.2, -354.6) * mm});
            skLineSegment(sketch, "E368", {"start": v(-203.2, -354.6) * mm, "end": v(-210.02, -306.09) * mm});
            skLineSegment(sketch, "E369", {"start": v(-210.02, -306.09) * mm, "end": v(-216.07, -306.93) * mm});
            skLineSegment(sketch, "E370", {"start": v(-216.07, -306.93) * mm, "end": v(-222.05, -264.35) * mm});
            skLineSegment(sketch, "E371", {"start": v(-222.05, -264.35) * mm, "end": v(-222.05, -58.35) * mm});
            skPoint(sketch, "E372.firstSnap0", {"position": v(-214.25, -234.44) * mm});
            skLineSegment(sketch, "E372.bottom", {"start": v(-214.25, -231.15) * mm, "end": v(-201.05, -231.15) * mm});
            skLineSegment(sketch, "E372.top", {"start": v(-214.25, -237.35) * mm, "end": v(-201.05, -237.35) * mm});
            skLineSegment(sketch, "E372.left", {"start": v(-214.25, -231.15) * mm, "end": v(-214.25, -237.35) * mm});
            skLineSegment(sketch, "E372.right", {"start": v(-201.05, -231.15) * mm, "end": v(-201.05, -237.35) * mm});
            skSolve(sketch);
        }
        {
            var Q0;
            Q0=makeQuery(id+"F8.imprint","IMPRINT",FACE,{"disambiguationData":[TD([[makeQuery(id+"F8.imprint","IMPRINT",EDGE,{"derivedFrom":sQuery(id+"F8.wireOp",EDGE,"E358")}),-1.0]])]});
            var Q1;
            Q1=sQuery(id+"F8.wireOp",EDGE,"7438bf09-0ed9-468e-8b2c-2fedd026e42d");
            var Q2;
            Q2=sQuery(id+"F8.wireOp",EDGE,"3aafcc7c-c0d7-41f1-a504-d8ca9cf4fa8c");
            var Q3;
            Q3=sQuery(id+"F8.wireOp",EDGE,"E361");
            var Q4;
            Q4=sQuery(id+"F8.wireOp",EDGE,"16cef16d-aa2a-4831-85ab-7757927928a5");
            var Q5;
            Q5=sQuery(id+"F8.wireOp",EDGE,"05f39b80-b350-4a29-a692-f4c906d76b01");
            var Q6;
            Q6=sQuery(id+"F8.wireOp",EDGE,"eb707996-bc03-4413-a1a1-6e94b0615dfa");
            var Q7;
            Q7=sQuery(id+"F8.wireOp",EDGE,"e63b45b1-e96b-43d0-90ce-ea5f1797e1ee");
            var Q8;
            Q8=sQuery(id+"F8.wireOp",EDGE,"3adf76c0-8028-45eb-829b-38d68a9c2f1a");
            var Q9;
            Q9=sQuery(id+"F8.wireOp",EDGE,"3d828959-db25-478d-95e0-5810f881a84a");
            var Q10;
            Q10=sQuery(id+"F8.wireOp",EDGE,"47fa3d6e-032f-4074-98a3-f5ecf73d1f24");
            var Q11;
            Q11=sQuery(id+"F8.wireOp",EDGE,"17e1d4b3-66ed-48b7-aa99-e94df9d1f9ae");
            var Q12;
            Q12=sQuery(id+"F8.wireOp",EDGE,"0559bfd0-5c5f-47af-afd2-249c3ebb3c19");
            var Q13;
            Q13=sQuery(id+"F8.wireOp",EDGE,"0733d196-948e-4033-b0eb-c96084580b2d");
            var Q14;
            Q14=sQuery(id+"F8.wireOp",EDGE,"35fb4cef-1b7b-4ec3-bf5f-a3259285bca5");
            var Q15;
            Q15=sQuery(id+"F8.wireOp",EDGE,"987bd6e0-6f39-4dbf-86b0-41abac857fc9");
            var Q16;
            Q16=sQuery(id+"F8.wireOp",EDGE,"6ea1534f-02f5-4238-88c3-00bdb9cfe0db");
            var Q17;
            Q17=sQuery(id+"F8.wireOp",EDGE,"53051bdd-1944-4d36-8c23-4ea97131240a");
            var Q18;
            Q18=sQuery(id+"F8.wireOp",EDGE,"9677cc2b-b3c7-4aa9-adbb-47640186b474");
            var Q19;
            Q19=sQuery(id+"F8.wireOp",EDGE,"b6c50380-3687-4c6d-9347-2a9d11bf2311");
            var Q20;
            Q20=sQuery(id+"F8.wireOp",EDGE,"c437b301-581c-4a8f-82dd-7a8338f74f7c");
            var Q21;
            Q21=sQuery(id+"F8.wireOp",EDGE,"e62d2b81-d5cb-465f-a852-fc36da86efd1");
            var Q22;
            Q22=sQuery(id+"F8.wireOp",EDGE,"95efe4b7-f27a-499f-b238-c583f8663a86");
            var Q23;
            Q23=sQuery(id+"F8.wireOp",EDGE,"0d9ced54-710c-4b45-853e-226535cb5607");
            var Q24;
            Q24=sQuery(id+"F8.wireOp",EDGE,"957b0021-b494-4d2e-836a-0bc290bfb905");
            var Q25;
            Q25=sQuery(id+"F8.wireOp",EDGE,"E369");
            var Q26;
            Q26=sQuery(id+"F8.wireOp",EDGE,"b23b0bcf-4c10-4b1e-bc59-4ef79bf87c30");
            var Q27;
            Q27=sQuery(id+"F8.wireOp",EDGE,"acff7ac1-f65d-4c27-80a0-cc79dc494d71");
            var Q28;
            Q28=sQuery(id+"F8.wireOp",EDGE,"a33ca7c8-6332-4fe2-a639-0e530abe665c");
            var Q29;
            Q29=sQuery(id+"F8.wireOp",EDGE,"d20e5261-bfb1-4a47-833e-bd09e8b20d8d");
            var Q30;
            Q30=sQuery(id+"F8.wireOp",EDGE,"8d43952c-6f44-43b3-95ff-e5da5c6f484c");
            var Q31;
            Q31=sQuery(id+"F8.wireOp",EDGE,"E370");
            var Q32;
            Q32=sQuery(id+"F8.wireOp",EDGE,"a90edf6c-e18f-48bf-9e5c-fcf47dc659e8");
            var Q33;
            Q33=sQuery(id+"F8.wireOp",EDGE,"E364");
            var Q34;
            Q34=sQuery(id+"F8.wireOp",EDGE,"bdba6fad-f2cf-4801-9f34-088b3d9808d7");
            var Q35;
            Q35=sQuery(id+"F8.wireOp",EDGE,"8c8a983a-0ca4-46f3-9a95-0f596a2f3925");
            var Q36;
            Q36=sQuery(id+"F8.wireOp",EDGE,"26b72eec-1faa-4247-9738-6ad77ad6c712");
            var Q37;
            Q37=sQuery(id+"F8.wireOp",EDGE,"a7997e96-d48f-4128-8119-14d12b6fe8f1");
            var Q38;
            Q38=sQuery(id+"F8.wireOp",EDGE,"32fe77c5-75f7-40c9-80fc-a071c57e77d3");
            var Q39;
            Q39=sQuery(id+"F8.wireOp",EDGE,"c831eab3-1ddb-43bd-a570-3deb294f97ad");
            var Q40;
            Q40=sQuery(id+"F8.wireOp",EDGE,"fddd3955-9666-44a3-9b1c-9ec49ec280b2");
            var Q41;
            Q41=sQuery(id+"F8.wireOp",EDGE,"eab2e40d-8d63-47cb-9180-8aa5334d36c8");
            var Q42;
            Q42=sQuery(id+"F8.wireOp",EDGE,"3de3d8ee-3cc9-4856-b5b7-a33e23e5e277");
            var Q43;
            Q43=sQuery(id+"F8.wireOp",EDGE,"db395a51-18d0-4e6f-a6c6-26124c5e73a4");
            var Q44;
            Q44=sQuery(id+"F8.wireOp",EDGE,"841e6fc5-233a-48fa-9c3b-ef678c0c9949");
            var Q45;
            Q45=sQuery(id+"F8.wireOp",EDGE,"0bc0d42e-ce25-48ba-b76c-88ebbf15afce");
            var Q46;
            Q46=sQuery(id+"F8.wireOp",EDGE,"e6ddcb83-0db2-4863-96cd-75a441d22157");
            var Q47;
            Q47=sQuery(id+"F8.wireOp",EDGE,"76622c80-285a-4397-9c80-98e5ae2619d5");
            var Q48;
            Q48=sQuery(id+"F8.wireOp",EDGE,"8000cce6-df33-4731-a850-a8edfbcc5cf6");
            var Q49;
            Q49=sQuery(id+"F8.wireOp",EDGE,"0b45788e-a51f-444d-8ee3-9e2438992d16");
            var Q50;
            Q50=sQuery(id+"F8.wireOp",EDGE,"17d1fd61-8404-4636-b5c0-5dedd580182a");
            var Q51;
            Q51=sQuery(id+"F8.wireOp",EDGE,"9ff2506d-78aa-4484-b4cb-46bbee655526");
            var Q52;
            Q52=sQuery(id+"F8.wireOp",EDGE,"9e18c8d1-750c-47cb-8223-5515a29932ba");
            var Q53;
            Q53=sQuery(id+"F8.wireOp",EDGE,"4b4cc33a-012a-4e24-bf6c-f82725983423");
            var Q54;
            Q54=sQuery(id+"F8.wireOp",EDGE,"412c5c57-279d-4684-9e46-71ae7460263c");
            var Q55;
            Q55=sQuery(id+"F8.wireOp",EDGE,"66e1d1ce-cfc9-480d-b9b1-9150ccd821b0");
            var Q56;
            Q56=sQuery(id+"F8.wireOp",EDGE,"05dbb808-0269-4816-a23a-24c2f0f6a21a");
            var Q57;
            Q57=sQuery(id+"F8.wireOp",EDGE,"e31d0fff-22f5-48d1-9521-f0bb79139697");
            var Q58;
            Q58=sQuery(id+"F8.wireOp",EDGE,"42dfa988-ea81-42c8-8470-0237ff7a31fe");
            var Q59;
            Q59=sQuery(id+"F8.wireOp",EDGE,"9d9f8bad-a807-421d-9bc9-f3170cb8e8b2");
            var Q60;
            Q60=sQuery(id+"F8.wireOp",EDGE,"60b80e6a-4438-4cf5-91ce-c7011a5a615c");
            var Q61;
            Q61=sQuery(id+"F8.wireOp",EDGE,"358aab23-7828-43db-ba55-f0d6291b6bdd");
            var Q62;
            Q62=sQuery(id+"F8.wireOp",EDGE,"dfadd18f-30fd-4097-88d2-087170952ccc");
            var Q63;
            Q63=sQuery(id+"F8.wireOp",EDGE,"40f6df7c-d692-4ce8-97a5-13a8ab7239cd");
            var Q64;
            Q64=sQuery(id+"F8.wireOp",EDGE,"656bc291-789f-47b0-8574-e0aff697a9b3");
            var Q65;
            Q65=sQuery(id+"F8.wireOp",EDGE,"243f8913-bb0e-4942-b72d-c3b885cc5abb");
            var Q66;
            Q66=sQuery(id+"F8.wireOp",EDGE,"77f4605c-31c9-415c-b50e-1a9bf2d671e8");
            var Q67;
            Q67=sQuery(id+"F8.wireOp",EDGE,"33218fb4-a357-4901-bbba-69cd955cb8a2");
            var Q68;
            Q68=sQuery(id+"F8.wireOp",EDGE,"89e6c438-db4d-466f-a11f-425bbfe35c23");
            var Q69;
            Q69=sQuery(id+"F8.wireOp",EDGE,"bd21f388-ce49-4e8e-b63c-f679b5b5b1d6");
            var Q70;
            Q70=sQuery(id+"F8.wireOp",EDGE,"7cb9c70f-7355-4b60-861e-27f03a55f4d8");
            var Q71;
            Q71=sQuery(id+"F8.wireOp",EDGE,"9afd0137-6df0-43e1-9d2b-496f239ad901");
            var Q72;
            Q72=sQuery(id+"F8.wireOp",EDGE,"b9212e23-c3d0-44e0-a787-992aafb23ba2");
            var Q73;
            Q73=sQuery(id+"F8.wireOp",EDGE,"f4c28886-9bcb-4a8f-a9be-aa85abba2385");
            var Q74;
            Q74=sQuery(id+"F8.wireOp",EDGE,"f0512903-8495-46d0-b665-5d8086a9fb55");
            var Q75;
            Q75=sQuery(id+"F8.wireOp",EDGE,"98423737-a051-4719-a072-267d69671e2e");
            var Q76;
            Q76=sQuery(id+"F8.wireOp",EDGE,"54498e13-3c17-4e90-87d4-50e1e80c9031");
            var Q77;
            Q77=sQuery(id+"F8.wireOp",EDGE,"5f74bce6-b83f-4ac1-ba8f-bc5dad9c900c");
            var Q78;
            Q78=sQuery(id+"F8.wireOp",EDGE,"f3a7a115-545d-4789-babe-ba925f936a5c");
            var Q79;
            Q79=sQuery(id+"F8.wireOp",EDGE,"a9402d29-55a6-46df-96ee-16d9f4be9a51");
            var Q80;
            Q80=sQuery(id+"F8.wireOp",EDGE,"239883c3-610c-4944-ac9b-02991acacd47");
            var Q81;
            Q81=sQuery(id+"F8.wireOp",EDGE,"d42c1468-3a16-4fd2-b5a7-de5339a6855c");
            var Q82;
            Q82=sQuery(id+"F8.wireOp",EDGE,"83698eaf-a3fb-4e35-9230-a32aadde8143");
            var Q83;
            Q83=sQuery(id+"F8.wireOp",EDGE,"f9db1889-c0aa-43d3-9449-9d0700c76474");
            var Q84;
            Q84=sQuery(id+"F8.wireOp",EDGE,"c86abe06-3697-4323-84c2-b67a276153e7");
            var Q85;
            Q85=sQuery(id+"F8.wireOp",EDGE,"5eccb832-b8a8-417e-9491-aa86088997fe");
            var Q86;
            Q86=sQuery(id+"F8.wireOp",EDGE,"E363");
            var Q87;
            Q87=sQuery(id+"F8.wireOp",EDGE,"14b7453d-e5dc-4819-9795-0435104b9672");
            var Q88;
            Q88=sQuery(id+"F8.wireOp",EDGE,"acd5b1ec-e645-4d41-ac5c-72b016f60b15");
            var Q89;
            Q89=sQuery(id+"F8.wireOp",EDGE,"83c6561b-0e4a-41e6-a382-3ea0aeb75a37");
            var Q90;
            Q90=sQuery(id+"F8.wireOp",EDGE,"f9c758ce-66bd-4c50-b33b-1f5b9be24108");
            var Q91;
            Q91=sQuery(id+"F8.wireOp",EDGE,"5eb54df9-5729-494b-82c0-7871c76fe49e");
            var Q92;
            Q92=sQuery(id+"F8.wireOp",EDGE,"ce9b9881-2537-4501-a9cd-2f9f18c17a14");
            var Q93;
            Q93=sQuery(id+"F8.wireOp",EDGE,"67800042-3790-43ee-9208-78fd7cca2e8b");
            var Q94;
            Q94=sQuery(id+"F8.wireOp",EDGE,"3ff9a71f-dd78-4f7e-9fcb-8b98933ee786");
            var Q95;
            Q95=sQuery(id+"F8.wireOp",EDGE,"db845659-5dd5-4aa2-be9c-c8e48df7cfda");
            var Q96;
            Q96=sQuery(id+"F8.wireOp",EDGE,"405e71eb-0479-43fc-a52b-594070f59d9b");
            var Q97;
            Q97=sQuery(id+"F8.wireOp",EDGE,"c7e6efcd-0038-4d41-9acc-186256c1fcfa");
            var Q98;
            Q98=sQuery(id+"F8.wireOp",EDGE,"179d42ab-f012-4eb8-b927-0c6d1ea908b3");
            var Q99;
            Q99=sQuery(id+"F8.wireOp",EDGE,"6b186893-37eb-4d53-b602-49ae6fa55cb7");
            var Q100;
            Q100=sQuery(id+"F8.wireOp",EDGE,"cef2fb56-6353-4ac8-8111-c46196b857a3");
            var Q101;
            Q101=sQuery(id+"F8.wireOp",EDGE,"a60746b8-7891-4439-b51b-4ee826248830");
            var Q102;
            Q102=sQuery(id+"F8.wireOp",EDGE,"83ffacfe-64e3-475c-ab98-4fd5824c749e");
            var Q103;
            Q103=sQuery(id+"F8.wireOp",EDGE,"445e4c82-d22c-45c9-be8d-9f38658914d0");
            var Q104;
            Q104=sQuery(id+"F8.wireOp",EDGE,"402e8568-db2e-4a06-88fe-23f8c4199e93");
            var Q105;
            Q105=sQuery(id+"F8.wireOp",EDGE,"73c01a1f-9f7c-4f93-a12f-6ed7271e34c8");
            var Q106;
            Q106=sQuery(id+"F8.wireOp",EDGE,"7b801e15-e81c-4ace-aa17-d9adca45a63b");
            var Q107;
            Q107=sQuery(id+"F8.wireOp",EDGE,"4016d545-c5ce-4dc5-8d40-90bc06a04896");
            var Q108;
            Q108=sQuery(id+"F8.wireOp",EDGE,"802dac81-a0d8-4e45-8bd0-41b4c898537b");
            var Q109;
            Q109=sQuery(id+"F8.wireOp",EDGE,"15f9dcfb-26e6-4022-9c5d-26aa09eb5faa");
            var Q110;
            Q110=sQuery(id+"F8.wireOp",EDGE,"3c74fbfc-fcd5-4768-8aef-082fea6d97b6");
            var Q111;
            Q111=sQuery(id+"F8.wireOp",EDGE,"65a31f0e-01cf-4b8b-9118-08d4ff0da5b8");
            var Q112;
            Q112=sQuery(id+"F8.wireOp",EDGE,"eaa008bd-9466-4210-aed3-a1157fd479ec");
            var Q113;
            Q113=sQuery(id+"F8.wireOp",EDGE,"b233208f-9283-4d25-9145-d0f946e8ceab");
            var Q114;
            Q114=sQuery(id+"F8.wireOp",EDGE,"E362");
            var Q115;
            Q115=sQuery(id+"F8.wireOp",EDGE,"0aea8f47-bffe-4659-8dcf-70e8338a7ee9");
            var Q116;
            Q116=sQuery(id+"F8.wireOp",EDGE,"d8da7c66-856a-4a65-8efd-74948bde30d6");
            var Q117;
            Q117=sQuery(id+"F8.wireOp",EDGE,"9c18de85-302e-42cc-87ef-be1ef258e208");
            var Q118;
            Q118=sQuery(id+"F8.wireOp",EDGE,"94491c61-c015-4a24-979a-1a8317bacdaa");
            var Q119;
            Q119=sQuery(id+"F8.wireOp",EDGE,"9d318716-0b97-45ae-a1c8-48018fa85e18");
            var Q120;
            Q120=sQuery(id+"F8.wireOp",EDGE,"E371");
            var Q121;
            Q121=sQuery(id+"F8.wireOp",EDGE,"E368");
            var Q122;
            Q122=sQuery(id+"F8.wireOp",EDGE,"E365");
            var Q123;
            Q123=sQuery(id+"F8.wireOp",EDGE,"3d95c97c-9a21-4ced-bfe6-38a337bfb64d");
            var Q124;
            Q124=sQuery(id+"F8.wireOp",EDGE,"E367");
            var Q125;
            Q125=sQuery(id+"F8.wireOp",EDGE,"E366");
            var Q126;
            Q126=sQuery(id+"F8.wireOp",EDGE,"1a7e7d5d-0da3-4086-bfbc-0ef366ae7fdf");
            var Q127;
            Q127=sQuery(id+"F8.wireOp",EDGE,"baf421a2-5d89-4bbc-8f43-0e9b74a2eae5");
            var Q128;
            Q128=sQuery(id+"F8.wireOp",EDGE,"E358");
            var Q129;
            Q129=sQuery(id+"F8.wireOp",EDGE,"d191dfa7-2023-43d3-86a8-d2be775a2da3");
            var Q130;
            Q130=sQuery(id+"F8.wireOp",EDGE,"E359");
            var Q131;
            Q131=sQuery(id+"F8.wireOp",EDGE,"E360");
            var Q132;
            Q132=sQuery(id+"F8.wireOp",EDGE,"0a3fd750-6602-442c-8aa6-b4dd949b677a");
            var Q133;
            Q133=sQuery(id+"F8.wireOp",EDGE,"edce4df4-00e4-485b-adac-6dd78fb67e5c");
            var Q134;
            Q134=sQuery(id+"F8.wireOp",EDGE,"5b6b5b7a-e76e-441c-ab03-f96a33d95e5a");
            var Q135;
            Q135=sQuery(id+"F8.wireOp",EDGE,"5fb030e9-5b69-44a1-85d0-a8f7533c1c15");
            var Q136;
            Q136=sQuery(id+"F8.wireOp",EDGE,"38312cf8-619d-408b-b8db-5fbd0d49f0b9");
            var Q137;
            Q137=sQuery(id+"F8.wireOp",EDGE,"7a0c552e-0003-44be-9e67-bb86d38640eb");
            var Q138;
            Q138=sQuery(id+"F8.wireOp",EDGE,"23f312bc-9320-43f0-8d57-69f00056f145");
            var Q139;
            Q139=sQuery(id+"F8.wireOp",EDGE,"4aabc4af-7752-405b-adb9-b1c7a156bcee");
            var Q140;
            Q140=sQuery(id+"F8.wireOp",EDGE,"be80d97b-d695-4206-8516-5feba4dd37db");
            var Q141;
            Q141=sQuery(id+"F8.wireOp",EDGE,"df0833c4-0da5-4ab2-a170-4a03aa4a239f");
            var Q142;
            Q142=sQuery(id+"F8.wireOp",EDGE,"71e8f440-5b08-4e64-a005-494dc38decce");
            var Q143;
            Q143=sQuery(id+"F8.wireOp",EDGE,"b2846d2c-a129-4702-a00e-9c1cd2a29976");
            var Q144;
            Q144=sQuery(id+"F8.wireOp",EDGE,"732de6c1-a08d-47a8-b5b7-bcb5918a560d");
            var Q145;
            Q145=sQuery(id+"F8.wireOp",EDGE,"1a562398-f58e-48e3-b501-083d8ca5e145");
            var Q146;
            Q146=sQuery(id+"F8.wireOp",EDGE,"ba572b4b-d95b-45e6-9a59-259a9878da60");
            var Q147;
            Q147=sQuery(id+"F8.wireOp",EDGE,"2fbb1810-931f-407f-bd4c-2f36580ad29b");
            var Q148;
            Q148=sQuery(id+"F8.wireOp",EDGE,"ea753efd-51d1-44a5-9cd5-43b4a5f08400");
            var Q149;
            Q149=sQuery(id+"F8.wireOp",EDGE,"9c749961-9a2f-4aa2-a9b4-1d88447fe5e5");
            var Q150;
            Q150=sQuery(id+"F8.wireOp",EDGE,"e4614eb8-6f63-4bef-8ae2-29212c6479b1");
            var Q151;
            Q151=sQuery(id+"F8.wireOp",EDGE,"0851ea0a-b94c-4b76-bca2-ed62650cb159");
            var Q152;
            Q152=sQuery(id+"F8.wireOp",EDGE,"9ec2006f-4d93-4ebe-aff4-f3130fe12eca");
            var Q153;
            Q153=sQuery(id+"F8.wireOp",EDGE,"c73d255b-b57e-4ac6-aa35-9fa95eddd9e2");
            var Q154;
            Q154=sQuery(id+"F8.wireOp",EDGE,"2b507933-040a-49a0-8801-199220a8f087");
            extrude(context, id + "F9", {"entities" : qUnion([Q0]), "surfaceEntities" : qUnion([Q1, Q2, Q3, Q4, Q5, Q6, Q7, Q8, Q9, Q10, Q11, Q12, Q13, Q14, Q15, Q16, Q17, Q18, Q19, Q20, Q21, Q22, Q23, Q24, Q25, Q26, Q27, Q28, Q29, Q30, Q31, Q32, Q33, Q34, Q35, Q36, Q37, Q38, Q39, Q40, Q41, Q42, Q43, Q44, Q45, Q46, Q47, Q48, Q49, Q50, Q51, Q52, Q53, Q54, Q55, Q56, Q57, Q58, Q59, Q60, Q61, Q62, Q63, Q64, Q65, Q66, Q67, Q68, Q69, Q70, Q71, Q72, Q73, Q74, Q75, Q76, Q77, Q78, Q79, Q80, Q81, Q82, Q83, Q84, Q85, Q86, Q87, Q88, Q89, Q90, Q91, Q92, Q93, Q94, Q95, Q96, Q97, Q98, Q99, Q100, Q101, Q102, Q103, Q104, Q105, Q106, Q107, Q108, Q109, Q110, Q111, Q112, Q113, Q114, Q115, Q116, Q117, Q118, Q119, Q120, Q121, Q122, Q123, Q124, Q125, Q126, Q127, Q128, Q129, Q130, Q131, Q132, Q133, Q134, Q135, Q136, Q137, Q138, Q139, Q140, Q141, Q142, Q143, Q144, Q145, Q146, Q147, Q148, Q149, Q150, Q151, Q152, Q153, Q154]), "depth" : 6 * mm});
        }
        {
            var Q0;
            Q0=qCreatedBy(makeId("Right.planeOp"),FACE);
            var sketch = newSketch(context, id + "F10", { "sketchPlane" : qUnion([Q0])});
            skLineSegment(sketch, "E373", {"start": v(23.59, -153.05) * mm, "end": v(23.56, -146.6) * mm});
            skLineSegment(sketch, "E374", {"start": v(23.56, -146.6) * mm, "end": v(23.46, -140.84) * mm});
            skLineSegment(sketch, "E375", {"start": v(23.46, -140.84) * mm, "end": v(23.3, -134.8) * mm});
            skLineSegment(sketch, "E376", {"start": v(23.3, -134.8) * mm, "end": v(23.07, -129.03) * mm});
            skLineSegment(sketch, "E377", {"start": v(23.07, -129.03) * mm, "end": v(22.8, -123.51) * mm});
            skLineSegment(sketch, "E378", {"start": v(22.8, -123.51) * mm, "end": v(22.46, -118.21) * mm});
            skLineSegment(sketch, "E379", {"start": v(22.46, -118.21) * mm, "end": v(22.08, -113.12) * mm});
            skLineSegment(sketch, "E380", {"start": v(22.08, -113.12) * mm, "end": v(21.65, -108.2) * mm});
            skLineSegment(sketch, "E381", {"start": v(21.65, -108.2) * mm, "end": v(21.18, -103.45) * mm});
            skLineSegment(sketch, "E382", {"start": v(21.18, -103.45) * mm, "end": v(20.67, -98.84) * mm});
            skLineSegment(sketch, "E383", {"start": v(20.67, -98.84) * mm, "end": v(20.12, -94.34) * mm});
            skLineSegment(sketch, "E384", {"start": v(20.12, -94.34) * mm, "end": v(19.54, -89.93) * mm});
            skLineSegment(sketch, "E385", {"start": v(19.54, -89.93) * mm, "end": v(18.93, -85.6) * mm});
            skLineSegment(sketch, "E386", {"start": v(18.93, -85.6) * mm, "end": v(18.3, -81.3) * mm});
            skLineSegment(sketch, "E387", {"start": v(18.3, -81.3) * mm, "end": v(17.64, -77.05) * mm});
            skLineSegment(sketch, "E388", {"start": v(17.64, -77.05) * mm, "end": v(16.96, -72.8) * mm});
            skLineSegment(sketch, "E389", {"start": v(16.96, -72.8) * mm, "end": v(16.27, -68.53) * mm});
            skLineSegment(sketch, "E390", {"start": v(16.27, -68.53) * mm, "end": v(15.56, -64.23) * mm});
            skLineSegment(sketch, "E391", {"start": v(15.56, -64.23) * mm, "end": v(14.84, -59.86) * mm});
            skLineSegment(sketch, "E392", {"start": v(14.84, -59.86) * mm, "end": v(14.12, -55.42) * mm});
            skLineSegment(sketch, "E393", {"start": v(14.12, -55.42) * mm, "end": v(13.3, -50.29) * mm});
            skLineSegment(sketch, "E394", {"start": v(13.3, -50.29) * mm, "end": v(2.58, -50.29) * mm});
            skLineSegment(sketch, "E395", {"start": v(2.58, -50.29) * mm, "end": v(2.58, -44.29) * mm});
            skLineSegment(sketch, "E396", {"start": v(2.58, -44.29) * mm, "end": v(-10.42, -44.29) * mm});
            skLineSegment(sketch, "E397", {"start": v(-10.42, -44.29) * mm, "end": v(-10.42, -50.29) * mm});
            skLineSegment(sketch, "E398", {"start": v(-10.42, -50.29) * mm, "end": v(-19.43, -50.29) * mm});
            skLineSegment(sketch, "E399", {"start": v(-19.43, -50.29) * mm, "end": v(-19.73, -153.05) * mm});
            skLineSegment(sketch, "E400", {"start": v(-19.73, -153.05) * mm, "end": v(-6.72, -153.05) * mm});
            skLineSegment(sketch, "E401", {"start": v(-6.72, -153.05) * mm, "end": v(-6.72, -159.05) * mm});
            skLineSegment(sketch, "E402", {"start": v(-6.72, -159.05) * mm, "end": v(9.28, -159.05) * mm});
            skLineSegment(sketch, "E403", {"start": v(9.28, -159.05) * mm, "end": v(9.28, -153.05) * mm});
            skLineSegment(sketch, "E404", {"start": v(9.28, -153.05) * mm, "end": v(23.59, -153.05) * mm});
            skCircle(sketch, "E405", {"center": v(-1.75, -73.16) * mm, "radius": 6.5 * mm});
            skCircle(sketch, "E406", {"center": v(2.42, -136.5) * mm, "radius": 6.5 * mm});
            skCircle(sketch, "E407", {"center": v(0.38, -106.6) * mm, "radius": 13.55 * mm});
            skSolve(sketch);
        }
        {
            var Q0;
            Q0=makeQuery(id+"F10.imprint","IMPRINT",FACE,{"disambiguationData":[TD([[makeQuery(id+"F10.imprint","IMPRINT",EDGE,{"derivedFrom":sQuery(id+"F10.wireOp",EDGE,"E373")}),1.0]])]});
            var Q1;
            Q1=sQuery(id+"F10.wireOp",EDGE,"df6008ed-a051-4d47-a5e0-54826faafe05");
            var Q2;
            Q2=sQuery(id+"F10.wireOp",EDGE,"4aab52d9-f22a-42d2-9842-7b8d7dc41e4d");
            var Q3;
            Q3=sQuery(id+"F10.wireOp",EDGE,"99a7cebe-3bda-4a04-a335-a0b0d8c074d6");
            var Q4;
            Q4=sQuery(id+"F10.wireOp",EDGE,"311a27a1-4f8a-4589-bfdb-7cc0b491bcc3");
            var Q5;
            Q5=sQuery(id+"F10.wireOp",EDGE,"f09b1a86-ca3b-4a2b-8f9e-649eae1fb8cc");
            var Q6;
            Q6=sQuery(id+"F10.wireOp",EDGE,"2453b2a5-d0b5-43f4-b4b4-002c1f81f17f");
            var Q7;
            Q7=sQuery(id+"F10.wireOp",EDGE,"E404");
            var Q8;
            Q8=sQuery(id+"F10.wireOp",EDGE,"b38a5d6e-5d86-474e-981f-acafcebce3c3");
            var Q9;
            Q9=sQuery(id+"F10.wireOp",EDGE,"034610c1-0392-4246-bad9-a8e4f61c5c7d");
            var Q10;
            Q10=sQuery(id+"F10.wireOp",EDGE,"c85a6e61-8205-45c6-9fa9-2acbeac23ffa");
            var Q11;
            Q11=sQuery(id+"F10.wireOp",EDGE,"99bc196f-a6e0-41fe-a4f5-2bd9828a5f02");
            var Q12;
            Q12=sQuery(id+"F10.wireOp",EDGE,"E403");
            var Q13;
            Q13=sQuery(id+"F10.wireOp",EDGE,"1ff903ac-96f8-4443-bd44-68e14abd6877");
            var Q14;
            Q14=sQuery(id+"F10.wireOp",EDGE,"E393");
            var Q15;
            Q15=sQuery(id+"F10.wireOp",EDGE,"e5c29a18-36f7-4658-b6df-5607aee5c342");
            var Q16;
            Q16=sQuery(id+"F10.wireOp",EDGE,"14d2577d-6a61-488f-af1f-bff5957020aa");
            var Q17;
            Q17=sQuery(id+"F10.wireOp",EDGE,"2e1310f0-926f-48a0-987c-c3db6df7d64e");
            var Q18;
            Q18=sQuery(id+"F10.wireOp",EDGE,"e1d10e58-86ad-4ab5-ba08-6e5e764f31cc");
            var Q19;
            Q19=sQuery(id+"F10.wireOp",EDGE,"4315923e-9dfb-4d60-97e0-23b195a91f12");
            var Q20;
            Q20=sQuery(id+"F10.wireOp",EDGE,"715c24cc-46b4-4173-b57a-72158d786902");
            var Q21;
            Q21=sQuery(id+"F10.wireOp",EDGE,"8a79b292-0d1c-44bd-a759-4333e274c866");
            var Q22;
            Q22=sQuery(id+"F10.wireOp",EDGE,"E392");
            var Q23;
            Q23=sQuery(id+"F10.wireOp",EDGE,"E399");
            var Q24;
            Q24=sQuery(id+"F10.wireOp",EDGE,"2a6618fc-7371-4049-95a4-033894ac797a");
            var Q25;
            Q25=sQuery(id+"F10.wireOp",EDGE,"E385");
            var Q26;
            Q26=sQuery(id+"F10.wireOp",EDGE,"E384");
            var Q27;
            Q27=sQuery(id+"F10.wireOp",EDGE,"b097f5e5-c586-4b81-ab87-f71c14d0c6e8");
            var Q28;
            Q28=sQuery(id+"F10.wireOp",EDGE,"ffe68139-52b2-43f8-9aba-82329a5452d4");
            var Q29;
            Q29=sQuery(id+"F10.wireOp",EDGE,"8246785e-1732-4e3d-8b6b-b35fe6324c91");
            var Q30;
            Q30=sQuery(id+"F10.wireOp",EDGE,"b6b491cd-635b-40b6-84a4-65ff6702402f");
            var Q31;
            Q31=sQuery(id+"F10.wireOp",EDGE,"E381");
            var Q32;
            Q32=sQuery(id+"F10.wireOp",EDGE,"E379");
            var Q33;
            Q33=sQuery(id+"F10.wireOp",EDGE,"E378");
            var Q34;
            Q34=sQuery(id+"F10.wireOp",EDGE,"1a487864-70be-4088-a417-9f59717e4192");
            var Q35;
            Q35=sQuery(id+"F10.wireOp",EDGE,"c7223a24-72f6-4173-922e-2b83a5160039");
            var Q36;
            Q36=sQuery(id+"F10.wireOp",EDGE,"E377");
            var Q37;
            Q37=sQuery(id+"F10.wireOp",EDGE,"E376");
            var Q38;
            Q38=sQuery(id+"F10.wireOp",EDGE,"cfb56b44-595d-42c9-b37e-3c9b9edc13a4");
            var Q39;
            Q39=sQuery(id+"F10.wireOp",EDGE,"E375");
            var Q40;
            Q40=sQuery(id+"F10.wireOp",EDGE,"E374");
            var Q41;
            Q41=sQuery(id+"F10.wireOp",EDGE,"E373");
            var Q42;
            Q42=sQuery(id+"F10.wireOp",EDGE,"E388");
            var Q43;
            Q43=sQuery(id+"F10.wireOp",EDGE,"E387");
            var Q44;
            Q44=sQuery(id+"F10.wireOp",EDGE,"E386");
            var Q45;
            Q45=sQuery(id+"F10.wireOp",EDGE,"71aa5af2-dbd0-43f2-aa0e-f85391708fd8");
            var Q46;
            Q46=sQuery(id+"F10.wireOp",EDGE,"c345046d-00ab-4499-8c25-581e4251e958");
            var Q47;
            Q47=sQuery(id+"F10.wireOp",EDGE,"E391");
            var Q48;
            Q48=sQuery(id+"F10.wireOp",EDGE,"E400");
            var Q49;
            Q49=sQuery(id+"F10.wireOp",EDGE,"18bf2ef7-141f-47db-8ab3-3b7bbd0167f8");
            var Q50;
            Q50=sQuery(id+"F10.wireOp",EDGE,"ab90d705-b435-4226-b4ab-af0c7c6a816c");
            var Q51;
            Q51=sQuery(id+"F10.wireOp",EDGE,"48cbb08e-5482-4876-95dc-ea5b059cfaf1");
            var Q52;
            Q52=sQuery(id+"F10.wireOp",EDGE,"e2851540-9acd-4b6c-947d-c1e00ef98f4a");
            var Q53;
            Q53=sQuery(id+"F10.wireOp",EDGE,"15baa296-5d44-43e0-be96-ab7d89d5b541");
            var Q54;
            Q54=sQuery(id+"F10.wireOp",EDGE,"E390");
            var Q55;
            Q55=sQuery(id+"F10.wireOp",EDGE,"E398");
            var Q56;
            Q56=sQuery(id+"F10.wireOp",EDGE,"697b80ca-f8c1-4887-98f0-f0a31d59261f");
            var Q57;
            Q57=sQuery(id+"F10.wireOp",EDGE,"E394");
            var Q58;
            Q58=sQuery(id+"F10.wireOp",EDGE,"d9333e0e-197e-47db-abf1-f60608d0edd2");
            var Q59;
            Q59=sQuery(id+"F10.wireOp",EDGE,"aed67ef2-7bc1-4602-bbc0-c9c2203b89cb");
            var Q60;
            Q60=sQuery(id+"F10.wireOp",EDGE,"8f5d825d-5ba5-42f1-8aab-c99a79372acb");
            var Q61;
            Q61=sQuery(id+"F10.wireOp",EDGE,"46fa9efe-99d3-4bec-bcd5-b417549a4774");
            var Q62;
            Q62=sQuery(id+"F10.wireOp",EDGE,"5000f96d-d63f-4ab5-b9ac-fe50d6e5173a");
            var Q63;
            Q63=sQuery(id+"F10.wireOp",EDGE,"68695924-987a-4bbd-8bed-cc8d4a2326dc");
            var Q64;
            Q64=sQuery(id+"F10.wireOp",EDGE,"E389");
            var Q65;
            Q65=sQuery(id+"F10.wireOp",EDGE,"e254e519-ea36-44a3-9a1a-265337d3eaba");
            var Q66;
            Q66=sQuery(id+"F10.wireOp",EDGE,"3902e6e8-5a04-4f2b-b47c-88c6d249a95d");
            var Q67;
            Q67=sQuery(id+"F10.wireOp",EDGE,"563c3c1c-4abd-4f95-9c55-cddcd1b673ca");
            var Q68;
            Q68=sQuery(id+"F10.wireOp",EDGE,"f364b375-443a-404e-918d-55794d1a4bc3");
            var Q69;
            Q69=sQuery(id+"F10.wireOp",EDGE,"e6c0b5ae-50cd-4df3-a7bf-bda815fab967");
            var Q70;
            Q70=sQuery(id+"F10.wireOp",EDGE,"70c30bc0-95e0-433c-9b24-b2f3b1ba7043");
            var Q71;
            Q71=sQuery(id+"F10.wireOp",EDGE,"086c0e2a-f3d3-4cb7-9126-cc585569f4d5");
            var Q72;
            Q72=sQuery(id+"F10.wireOp",EDGE,"a5b58a6f-dfdf-4f45-b946-b4bc7691487a");
            var Q73;
            Q73=sQuery(id+"F10.wireOp",EDGE,"9613ccf7-1da0-4789-84ce-c4428d5e39d9");
            var Q74;
            Q74=sQuery(id+"F10.wireOp",EDGE,"4223f6de-9fa1-425a-914b-390431b13dc6");
            var Q75;
            Q75=sQuery(id+"F10.wireOp",EDGE,"aa4ae9dc-76f6-4bfe-acc6-054bc9cce284");
            var Q76;
            Q76=sQuery(id+"F10.wireOp",EDGE,"997a1789-beda-45dd-8c34-f36316137f0c");
            var Q77;
            Q77=sQuery(id+"F10.wireOp",EDGE,"e4467757-fcfa-4a1e-955a-8d98d37dd3b3");
            var Q78;
            Q78=sQuery(id+"F10.wireOp",EDGE,"E402");
            var Q79;
            Q79=sQuery(id+"F10.wireOp",EDGE,"c8d80b4a-54dc-4bf3-9fc4-148402600593");
            var Q80;
            Q80=sQuery(id+"F10.wireOp",EDGE,"6e6dc695-8d5a-423e-bafb-110ec7866d0d");
            var Q81;
            Q81=sQuery(id+"F10.wireOp",EDGE,"E401");
            var Q82;
            Q82=sQuery(id+"F10.wireOp",EDGE,"ee6eab2d-99ec-49f5-8976-9935124fb785");
            var Q83;
            Q83=sQuery(id+"F10.wireOp",EDGE,"03c14a15-2d52-42b9-b407-0266a3aaa21a");
            var Q84;
            Q84=sQuery(id+"F10.wireOp",EDGE,"E383");
            var Q85;
            Q85=sQuery(id+"F10.wireOp",EDGE,"E382");
            var Q86;
            Q86=sQuery(id+"F10.wireOp",EDGE,"a1d78ad1-a681-4b0e-a693-840445aa8a60");
            var Q87;
            Q87=sQuery(id+"F10.wireOp",EDGE,"75f659b3-f065-41c3-9b6c-62aa1dfc3626");
            var Q88;
            Q88=sQuery(id+"F10.wireOp",EDGE,"bc500679-e7f9-4753-b607-e6b4cfc43491");
            var Q89;
            Q89=sQuery(id+"F10.wireOp",EDGE,"a1bc20c7-b6b7-4139-90ab-e52d8f53e8d3");
            var Q90;
            Q90=sQuery(id+"F10.wireOp",EDGE,"a24ace28-f16b-4324-a77b-52cbeaaefa50");
            var Q91;
            Q91=sQuery(id+"F10.wireOp",EDGE,"eaa92fdc-50b9-458c-9052-80530391df5c");
            var Q92;
            Q92=sQuery(id+"F10.wireOp",EDGE,"aa8434d6-9d0c-4992-9488-60da6ff0b076");
            var Q93;
            Q93=sQuery(id+"F10.wireOp",EDGE,"6081b5e3-7536-410c-9549-21f6253b10f8");
            var Q94;
            Q94=sQuery(id+"F10.wireOp",EDGE,"b6c03adc-43af-4188-8eb4-61c2f9943089");
            var Q95;
            Q95=sQuery(id+"F10.wireOp",EDGE,"3fb12c79-37ad-4bbc-b812-7ed4e22b8ffe");
            var Q96;
            Q96=sQuery(id+"F10.wireOp",EDGE,"9293d1e2-d0a3-4edf-a87f-4647457a011f");
            var Q97;
            Q97=sQuery(id+"F10.wireOp",EDGE,"E397");
            var Q98;
            Q98=sQuery(id+"F10.wireOp",EDGE,"98277637-b986-4a37-80d3-d166ed591bcc");
            var Q99;
            Q99=sQuery(id+"F10.wireOp",EDGE,"5f5cdbe3-2675-441d-a431-80176a26b8d7");
            var Q100;
            Q100=sQuery(id+"F10.wireOp",EDGE,"ef703063-6deb-4866-8635-1b8ba32bd24a");
            var Q101;
            Q101=sQuery(id+"F10.wireOp",EDGE,"dc0c1875-f912-4633-a8b1-7cb8dcba3f55");
            var Q102;
            Q102=sQuery(id+"F10.wireOp",EDGE,"7a360095-b22f-4162-8155-58df822eba64");
            var Q103;
            Q103=sQuery(id+"F10.wireOp",EDGE,"0003aa31-896d-449c-9e29-ac0365c35be9");
            var Q104;
            Q104=sQuery(id+"F10.wireOp",EDGE,"b5eb19d4-8c1a-4931-a12e-3193c2ab18d8");
            var Q105;
            Q105=sQuery(id+"F10.wireOp",EDGE,"21f037c6-ea2c-4502-bdce-8eb16cf29b47");
            var Q106;
            Q106=sQuery(id+"F10.wireOp",EDGE,"9d300394-3b50-4ed0-959a-8a91df1d2114");
            var Q107;
            Q107=sQuery(id+"F10.wireOp",EDGE,"6f1ee71c-1ac3-4042-ad4e-a47ab9d57c65");
            var Q108;
            Q108=sQuery(id+"F10.wireOp",EDGE,"E396");
            var Q109;
            Q109=sQuery(id+"F10.wireOp",EDGE,"fe34e1c3-73cd-4da9-a8b6-71a62420cdb1");
            var Q110;
            Q110=sQuery(id+"F10.wireOp",EDGE,"0e1bdaa7-645e-4d8b-b6f2-6b7b79c2be32");
            var Q111;
            Q111=sQuery(id+"F10.wireOp",EDGE,"E395");
            var Q112;
            Q112=sQuery(id+"F10.wireOp",EDGE,"E380");
            var Q113;
            Q113=sQuery(id+"F10.wireOp",EDGE,"92327432-6dc6-4a4b-bb3f-3de9e4816187");
            extrude(context, id + "F11", {"entities" : qUnion([Q0]), "surfaceEntities" : qUnion([Q1, Q2, Q3, Q4, Q5, Q6, Q7, Q8, Q9, Q10, Q11, Q12, Q13, Q14, Q15, Q16, Q17, Q18, Q19, Q20, Q21, Q22, Q23, Q24, Q25, Q26, Q27, Q28, Q29, Q30, Q31, Q32, Q33, Q34, Q35, Q36, Q37, Q38, Q39, Q40, Q41, Q42, Q43, Q44, Q45, Q46, Q47, Q48, Q49, Q50, Q51, Q52, Q53, Q54, Q55, Q56, Q57, Q58, Q59, Q60, Q61, Q62, Q63, Q64, Q65, Q66, Q67, Q68, Q69, Q70, Q71, Q72, Q73, Q74, Q75, Q76, Q77, Q78, Q79, Q80, Q81, Q82, Q83, Q84, Q85, Q86, Q87, Q88, Q89, Q90, Q91, Q92, Q93, Q94, Q95, Q96, Q97, Q98, Q99, Q100, Q101, Q102, Q103, Q104, Q105, Q106, Q107, Q108, Q109, Q110, Q111, Q112, Q113]), "oppositeDirection" : true, "depth" : 3 * mm});
        }
        {
            var Q0;
            Q0=qCreatedBy(makeId("Right.planeOp"),FACE);
            var sketch = newSketch(context, id + "F12", { "sketchPlane" : qUnion([Q0])});
            skLineSegment(sketch, "E408.bottom", {"start": v(-399.41, 705.57) * mm, "end": v(-393.41, 705.57) * mm});
            skLineSegment(sketch, "E408.top", {"start": v(-399.41, -350.43) * mm, "end": v(-393.41, -350.43) * mm});
            skLineSegment(sketch, "E408.left", {"start": v(-399.41, 705.57) * mm, "end": v(-399.41, -350.43) * mm});
            skLineSegment(sketch, "E408.right", {"start": v(-393.41, 705.57) * mm, "end": v(-393.41, -350.43) * mm});
            skSolve(sketch);
        }
        {
            var Q0;
            Q0 = qSketchRegion(id + "F12", true);
            extrude(context, id + "F13", {"entities" : qUnion([Q0]), "depth" : 9 * mm});
        }
        {
            var Q0;
            Q0=qCreatedBy(makeId("Right.planeOp"),FACE);
            var sketch = newSketch(context, id + "F14", { "sketchPlane" : qUnion([Q0])});
            skLineSegment(sketch, "E409.bottom", {"start": v(-441.79, 705.2) * mm, "end": v(-435.79, 705.2) * mm});
            skLineSegment(sketch, "E409.top", {"start": v(-441.79, -350.8) * mm, "end": v(-435.79, -350.8) * mm});
            skLineSegment(sketch, "E409.left", {"start": v(-441.79, 705.2) * mm, "end": v(-441.79, -350.8) * mm});
            skLineSegment(sketch, "E409.right", {"start": v(-435.79, 705.2) * mm, "end": v(-435.79, -350.8) * mm});
            skSolve(sketch);
        }
        {
            var Q0;
            Q0=makeQuery(id+"F14.imprint","IMPRINT",FACE,{"disambiguationData":[TD([[makeQuery(id+"F14.imprint","IMPRINT",EDGE,{"derivedFrom":sQuery(id+"F14.wireOp",EDGE,"E409.bottom")}),-1.0]])]});
            extrude(context, id + "F15", {"entities" : qUnion([Q0]), "depth" : 6 * mm});
        }
        {
            var Q0;
            Q0=qCreatedBy(makeId("Right.planeOp"),FACE);
            var sketch = newSketch(context, id + "F16", { "sketchPlane" : qUnion([Q0])});
            skLineSegment(sketch, "E410.0", {"start": v(-91.53, 79.66) * mm, "end": v(-96.34, 78.48) * mm});
            skLineSegment(sketch, "E410.1", {"start": v(-23.75, 94.27) * mm, "end": v(-28.12, 93.55) * mm});
            skLineSegment(sketch, "E410.2", {"start": v(52.86, 102.17) * mm, "end": v(46.82, 102) * mm});
            skCircle(sketch, "E410.3", {"center": v(48.53, 81.13) * mm, "radius": 6.5 * mm});
            skLineSegment(sketch, "E410.4", {"start": v(-96.34, 78.48) * mm, "end": v(-101.14, 77.28) * mm});
            skLineSegment(sketch, "E410.5", {"start": v(-28.12, 93.55) * mm, "end": v(-32.66, 92.83) * mm});
            skLineSegment(sketch, "E410.6", {"start": v(46.82, 102) * mm, "end": v(41.06, 101.78) * mm});
            skCircle(sketch, "E410.7", {"center": v(-14.82, 76.96) * mm, "radius": 6.5 * mm});
            skLineSegment(sketch, "E410.8", {"start": v(-101.14, 77.28) * mm, "end": v(-105.94, 76.07) * mm});
            skLineSegment(sketch, "E410.9", {"start": v(-32.66, 92.83) * mm, "end": v(-37.2, 92.1) * mm});
            skLineSegment(sketch, "E410.10", {"start": v(41.06, 101.78) * mm, "end": v(35.53, 101.5) * mm});
            skLineSegment(sketch, "E410.11", {"start": v(104.53, 94.12) * mm, "end": v(100.47, 95.16) * mm});
            skLineSegment(sketch, "E410.14", {"start": v(-105.94, 76.07) * mm, "end": v(-110.73, 74.85) * mm});
            skLineSegment(sketch, "E410.15", {"start": v(-37.2, 92.1) * mm, "end": v(-37.2, 83.28) * mm});
            skLineSegment(sketch, "E410.16", {"start": v(35.53, 101.5) * mm, "end": v(30.24, 101.17) * mm});
            skLineSegment(sketch, "E410.17", {"start": v(100.47, 95.16) * mm, "end": v(98.76, 89.3) * mm});
            skLineSegment(sketch, "E410.18", {"start": v(-110.73, 74.85) * mm, "end": v(-115.52, 73.61) * mm});
            skLineSegment(sketch, "E410.19", {"start": v(-37.2, 83.28) * mm, "end": v(-43.4, 83.28) * mm});
            skLineSegment(sketch, "E410.20", {"start": v(30.24, 101.17) * mm, "end": v(25.14, 100.8) * mm});
            skLineSegment(sketch, "E410.21", {"start": v(98.76, 89.3) * mm, "end": v(92.83, 91.04) * mm});
            skLineSegment(sketch, "E410.22", {"start": v(-115.52, 73.61) * mm, "end": v(-120.3, 72.36) * mm});
            skLineSegment(sketch, "E410.23", {"start": v(-43.4, 83.28) * mm, "end": v(-43.4, 91.03) * mm});
            skLineSegment(sketch, "E410.24", {"start": v(25.14, 100.8) * mm, "end": v(20.23, 100.36) * mm});
            skLineSegment(sketch, "E410.25", {"start": v(92.83, 91.04) * mm, "end": v(94.63, 97.2) * mm});
            skLineSegment(sketch, "E410.26", {"start": v(134.32, 66.87) * mm, "end": v(130.67, 73.42) * mm});
            skLineSegment(sketch, "E410.27", {"start": v(-120.3, 72.36) * mm, "end": v(-125.08, 71.1) * mm});
            skLineSegment(sketch, "E410.28", {"start": v(-43.4, 91.03) * mm, "end": v(-48.14, 89.92) * mm});
            skLineSegment(sketch, "E410.29", {"start": v(20.23, 100.36) * mm, "end": v(15.48, 99.9) * mm});
            skLineSegment(sketch, "E410.30", {"start": v(94.63, 97.2) * mm, "end": v(90.15, 98.07) * mm});
            skLineSegment(sketch, "E410.31", {"start": v(-125.08, 71.1) * mm, "end": v(-129.85, 69.83) * mm});
            skLineSegment(sketch, "E410.32", {"start": v(-48.14, 89.92) * mm, "end": v(-52.97, 88.81) * mm});
            skLineSegment(sketch, "E410.33", {"start": v(15.48, 99.9) * mm, "end": v(10.86, 99.38) * mm});
            skLineSegment(sketch, "E410.34", {"start": v(90.15, 98.07) * mm, "end": v(85.63, 98.85) * mm});
            skLineSegment(sketch, "E410.35", {"start": v(-129.85, 69.83) * mm, "end": v(-133.37, 68.87) * mm});
            skLineSegment(sketch, "E410.36", {"start": v(-52.97, 88.81) * mm, "end": v(-57.8, 87.7) * mm});
            skLineSegment(sketch, "E410.37", {"start": v(10.86, 99.38) * mm, "end": v(6.36, 98.83) * mm});
            skLineSegment(sketch, "E410.38", {"start": v(85.63, 98.85) * mm, "end": v(80.98, 99.54) * mm});
            skLineSegment(sketch, "E410.40", {"start": v(-57.8, 87.7) * mm, "end": v(-62.63, 86.58) * mm});
            skLineSegment(sketch, "E410.41", {"start": v(6.36, 98.83) * mm, "end": v(1.95, 98.25) * mm});
            skLineSegment(sketch, "E410.42", {"start": v(80.98, 99.54) * mm, "end": v(76.61, 100.13) * mm});
            skLineSegment(sketch, "E410.43", {"start": v(1.95, 98.25) * mm, "end": v(-2.38, 97.64) * mm});
            skLineSegment(sketch, "E410.44", {"start": v(76.61, 100.13) * mm, "end": v(75.02, 100.31) * mm});
            skLineSegment(sketch, "E410.45", {"start": v(128.46, 81.7) * mm, "end": v(124.52, 84.4) * mm});
            skLineSegment(sketch, "E410.47", {"start": v(-62.63, 86.58) * mm, "end": v(-67.45, 85.45) * mm});
            skLineSegment(sketch, "E410.48", {"start": v(-2.38, 97.64) * mm, "end": v(-6.67, 97) * mm});
            skLineSegment(sketch, "E410.49", {"start": v(75.02, 100.31) * mm, "end": v(75.02, 93.91) * mm});
            skLineSegment(sketch, "E410.50", {"start": v(124.52, 84.4) * mm, "end": v(121.47, 79.12) * mm});
            skLineSegment(sketch, "E410.52", {"start": v(-67.45, 85.45) * mm, "end": v(-72.27, 84.3) * mm});
            skLineSegment(sketch, "E410.53", {"start": v(-6.67, 97) * mm, "end": v(-10.93, 96.35) * mm});
            skLineSegment(sketch, "E410.54", {"start": v(75.02, 93.91) * mm, "end": v(65.82, 93.91) * mm});
            skLineSegment(sketch, "E410.55", {"start": v(121.47, 79.12) * mm, "end": v(116.13, 82.2) * mm});
            skLineSegment(sketch, "E410.58", {"start": v(-10.93, 96.35) * mm, "end": v(-15.18, 95.67) * mm});
            skLineSegment(sketch, "E410.59", {"start": v(65.82, 93.91) * mm, "end": v(65.82, 102.3) * mm});
            skLineSegment(sketch, "E410.60", {"start": v(116.13, 82.2) * mm, "end": v(119.34, 87.78) * mm});
            skLineSegment(sketch, "E410.63", {"start": v(65.82, 102.3) * mm, "end": v(59.19, 102.27) * mm});
            skLineSegment(sketch, "E410.64", {"start": v(-81.9, 82) * mm, "end": v(-86.72, 80.84) * mm});
            skLineSegment(sketch, "E410.65", {"start": v(-19.45, 94.98) * mm, "end": v(-23.75, 94.27) * mm});
            skLineSegment(sketch, "E410.66", {"start": v(59.19, 102.27) * mm, "end": v(52.86, 102.17) * mm});
            skCircle(sketch, "E410.67", {"center": v(18.63, 79.1) * mm, "radius": 13.55 * mm});
            skLineSegment(sketch, "E410.68", {"start": v(-86.72, 80.84) * mm, "end": v(-91.53, 79.66) * mm});
            skLineSegment(sketch, "E410.69", {"start": v(111.6, 61.4) * mm, "end": v(116.68, 61.82) * mm});
            skLineSegment(sketch, "E410.70", {"start": v(116.68, 61.82) * mm, "end": v(121.05, 62.42) * mm});
            skLineSegment(sketch, "E410.71", {"start": v(-133.4, 59.6) * mm, "end": v(-43.4, 59.28) * mm});
            skLineSegment(sketch, "E410.72", {"start": v(-43.4, 59.28) * mm, "end": v(-43.4, 67.28) * mm});
            skLineSegment(sketch, "E410.73", {"start": v(-43.4, 67.28) * mm, "end": v(-37.2, 67.28) * mm});
            skLineSegment(sketch, "E410.74", {"start": v(-37.2, 67.28) * mm, "end": v(-37.2, 59.28) * mm});
            skLineSegment(sketch, "E410.75", {"start": v(-37.2, 59.28) * mm, "end": v(65.82, 58.98) * mm});
            skLineSegment(sketch, "E410.76", {"start": v(65.82, 58.98) * mm, "end": v(65.82, 67.11) * mm});
            skLineSegment(sketch, "E410.77", {"start": v(65.82, 67.11) * mm, "end": v(75.02, 67.11) * mm});
            skLineSegment(sketch, "E410.78", {"start": v(75.02, 67.11) * mm, "end": v(75.02, 60.73) * mm});
            skLineSegment(sketch, "E410.79", {"start": v(75.02, 60.74) * mm, "end": v(99.85, 60.81) * mm});
            skLineSegment(sketch, "E410.80", {"start": v(99.85, 60.81) * mm, "end": v(99.85, 67.06) * mm});
            skLineSegment(sketch, "E410.81", {"start": v(99.85, 67.06) * mm, "end": v(105.7, 67.06) * mm});
            skLineSegment(sketch, "E410.82", {"start": v(105.7, 67.06) * mm, "end": v(105.7, 61.14) * mm});
            skLineSegment(sketch, "E410.83", {"start": v(105.7, 61.14) * mm, "end": v(111.6, 61.4) * mm});
            skLineSegment(sketch, "E410.84", {"start": v(112.05, 91.25) * mm, "end": v(108.3, 92.8) * mm});
            skLineSegment(sketch, "E410.85", {"start": v(108.3, 92.8) * mm, "end": v(104.53, 94.12) * mm});
            skLineSegment(sketch, "E410.86", {"start": v(124.86, 63.23) * mm, "end": v(128.31, 64.27) * mm});
            skLineSegment(sketch, "E410.87", {"start": v(128.31, 64.27) * mm, "end": v(131.85, 65.67) * mm});
            skLineSegment(sketch, "E410.88", {"start": v(131.85, 65.67) * mm, "end": v(134.32, 66.87) * mm});
            skLineSegment(sketch, "E410.89", {"start": v(130.67, 73.42) * mm, "end": v(134.6, 75.6) * mm});
            skLineSegment(sketch, "E410.90", {"start": v(134.6, 75.6) * mm, "end": v(132.03, 78.53) * mm});
            skLineSegment(sketch, "E410.91", {"start": v(132.03, 78.53) * mm, "end": v(128.46, 81.7) * mm});
            skLineSegment(sketch, "E410.92", {"start": v(-15.18, 95.67) * mm, "end": v(-19.45, 94.98) * mm});
            skLineSegment(sketch, "E410.93", {"start": v(119.34, 87.78) * mm, "end": v(115.72, 89.55) * mm});
            skLineSegment(sketch, "E410.95", {"start": v(115.72, 89.55) * mm, "end": v(112.05, 91.25) * mm});
            skLineSegment(sketch, "E410.96", {"start": v(121.05, 62.42) * mm, "end": v(124.86, 63.23) * mm});
            skLineSegment(sketch, "E411", {"start": v(-133.4, 59.6) * mm, "end": v(-133.37, 68.87) * mm});
            skLineSegment(sketch, "E412", {"start": v(-81.9, 82) * mm, "end": v(-72.27, 84.3) * mm});
            skSolve(sketch);
        }
        {
            var Q0;
            Q0=makeQuery(id+"F16.imprint","IMPRINT",FACE,{"disambiguationData":[TD([[makeQuery(id+"F16.imprint","IMPRINT",EDGE,{"derivedFrom":sQuery(id+"F16.wireOp",EDGE,"E410.0")}),1.0]])]});
            extrude(context, id + "F17", {"entities" : qUnion([Q0]), "depth" : 3 * mm});
        }
        {
            var Q0;
            Q0=qCreatedBy(makeId("Right.planeOp"),FACE);
            var sketch = newSketch(context, id + "F18", { "sketchPlane" : qUnion([Q0])});
            skLineSegment(sketch, "E413.1", {"start": v(41.06, 101.78) * mm, "end": v(35.53, 101.5) * mm});
            skCircle(sketch, "E413.2", {"center": v(-14.82, 76.96) * mm, "radius": 6.5 * mm});
            skLineSegment(sketch, "E413.3", {"start": v(46.82, 102) * mm, "end": v(41.06, 101.78) * mm});
            skLineSegment(sketch, "E413.4", {"start": v(-28.12, 93.55) * mm, "end": v(-32.66, 92.83) * mm});
            skLineSegment(sketch, "E413.5", {"start": v(-96.34, 78.48) * mm, "end": v(-101.14, 77.28) * mm});
            skCircle(sketch, "E413.6", {"center": v(48.53, 81.13) * mm, "radius": 6.5 * mm});
            skLineSegment(sketch, "E413.7", {"start": v(52.86, 102.17) * mm, "end": v(46.82, 102) * mm});
            skLineSegment(sketch, "E413.8", {"start": v(-91.53, 79.66) * mm, "end": v(-96.34, 78.48) * mm});
            skLineSegment(sketch, "E413.9", {"start": v(100.47, 95.16) * mm, "end": v(98.76, 89.3) * mm});
            skLineSegment(sketch, "E413.10", {"start": v(35.53, 101.5) * mm, "end": v(30.24, 101.17) * mm});
            skLineSegment(sketch, "E413.11", {"start": v(-37.2, 92.1) * mm, "end": v(-37.2, 83.28) * mm});
            skLineSegment(sketch, "E413.12", {"start": v(111.6, 61.4) * mm, "end": v(116.68, 61.82) * mm});
            skLineSegment(sketch, "E413.13", {"start": v(94.63, 97.2) * mm, "end": v(90.15, 98.07) * mm});
            skLineSegment(sketch, "E413.14", {"start": v(-2.38, 97.64) * mm, "end": v(-6.67, 97) * mm});
            skLineSegment(sketch, "E413.15", {"start": v(-86.72, 80.84) * mm, "end": v(-91.53, 79.66) * mm});
            skLineSegment(sketch, "E413.16", {"start": v(20.23, 100.36) * mm, "end": v(15.48, 99.9) * mm});
            skLineSegment(sketch, "E413.17", {"start": v(-62.63, 86.58) * mm, "end": v(-67.45, 85.45) * mm});
            skCircle(sketch, "E413.18", {"center": v(18.63, 79.1) * mm, "radius": 13.55 * mm});
            skLineSegment(sketch, "E413.19", {"start": v(105.7, 61.14) * mm, "end": v(111.6, 61.4) * mm});
            skLineSegment(sketch, "E413.20", {"start": v(59.19, 102.27) * mm, "end": v(52.86, 102.17) * mm});
            skLineSegment(sketch, "E413.21", {"start": v(105.7, 67.06) * mm, "end": v(105.7, 61.14) * mm});
            skLineSegment(sketch, "E413.23", {"start": v(99.85, 67.06) * mm, "end": v(105.7, 67.06) * mm});
            skLineSegment(sketch, "E413.24", {"start": v(-81.9, 82) * mm, "end": v(-72.27, 84.3) * mm});
            skLineSegment(sketch, "E413.25", {"start": v(134.32, 66.87) * mm, "end": v(130.67, 73.42) * mm});
            skLineSegment(sketch, "E413.26", {"start": v(-81.9, 82) * mm, "end": v(-86.72, 80.84) * mm});
            skLineSegment(sketch, "E413.27", {"start": v(99.85, 60.81) * mm, "end": v(99.85, 67.06) * mm});
            skLineSegment(sketch, "E413.29", {"start": v(92.83, 91.04) * mm, "end": v(94.63, 97.2) * mm});
            skLineSegment(sketch, "E413.30", {"start": v(25.14, 100.8) * mm, "end": v(20.23, 100.36) * mm});
            skLineSegment(sketch, "E413.31", {"start": v(65.82, 102.3) * mm, "end": v(59.19, 102.27) * mm});
            skLineSegment(sketch, "E413.32", {"start": v(75.02, 60.74) * mm, "end": v(99.85, 60.81) * mm});
            skLineSegment(sketch, "E413.33", {"start": v(-43.4, 83.28) * mm, "end": v(-43.4, 91.03) * mm});
            skLineSegment(sketch, "E413.34", {"start": v(-57.8, 87.7) * mm, "end": v(-62.63, 86.58) * mm});
            skLineSegment(sketch, "E413.35", {"start": v(116.13, 82.2) * mm, "end": v(119.34, 87.78) * mm});
            skLineSegment(sketch, "E413.36", {"start": v(75.02, 67.11) * mm, "end": v(75.02, 60.73) * mm});
            skLineSegment(sketch, "E413.38", {"start": v(85.63, 98.85) * mm, "end": v(80.98, 99.54) * mm});
            skLineSegment(sketch, "E413.39", {"start": v(65.82, 93.91) * mm, "end": v(65.82, 102.3) * mm});
            skLineSegment(sketch, "E413.40", {"start": v(65.82, 67.11) * mm, "end": v(75.02, 67.11) * mm});
            skLineSegment(sketch, "E413.41", {"start": v(-15.18, 95.67) * mm, "end": v(-19.45, 94.98) * mm});
            skLineSegment(sketch, "E413.42", {"start": v(98.76, 89.3) * mm, "end": v(92.83, 91.04) * mm});
            skLineSegment(sketch, "E413.43", {"start": v(10.86, 99.38) * mm, "end": v(6.36, 98.83) * mm});
            skLineSegment(sketch, "E413.44", {"start": v(65.82, 58.98) * mm, "end": v(65.82, 67.11) * mm});
            skLineSegment(sketch, "E413.45", {"start": v(132.03, 78.53) * mm, "end": v(128.46, 81.7) * mm});
            skLineSegment(sketch, "E413.46", {"start": v(30.24, 101.17) * mm, "end": v(25.14, 100.8) * mm});
            skLineSegment(sketch, "E413.47", {"start": v(-52.97, 88.81) * mm, "end": v(-57.8, 87.7) * mm});
            skLineSegment(sketch, "E413.48", {"start": v(121.47, 79.12) * mm, "end": v(116.13, 82.2) * mm});
            skLineSegment(sketch, "E413.49", {"start": v(-37.2, 59.28) * mm, "end": v(65.82, 58.98) * mm});
            skLineSegment(sketch, "E413.50", {"start": v(-37.2, 83.28) * mm, "end": v(-43.4, 83.28) * mm});
            skLineSegment(sketch, "E413.51", {"start": v(75.02, 93.91) * mm, "end": v(65.82, 93.91) * mm});
            skLineSegment(sketch, "E413.52", {"start": v(-37.2, 67.28) * mm, "end": v(-37.2, 59.28) * mm});
            skLineSegment(sketch, "E413.54", {"start": v(-43.4, 67.28) * mm, "end": v(-37.2, 67.28) * mm});
            skLineSegment(sketch, "E413.55", {"start": v(-67.45, 85.45) * mm, "end": v(-72.27, 84.3) * mm});
            skLineSegment(sketch, "E413.56", {"start": v(-43.4, 59.28) * mm, "end": v(-43.4, 67.28) * mm});
            skLineSegment(sketch, "E413.57", {"start": v(-48.14, 89.92) * mm, "end": v(-52.97, 88.81) * mm});
            skLineSegment(sketch, "E413.58", {"start": v(124.52, 84.4) * mm, "end": v(121.47, 79.12) * mm});
            skLineSegment(sketch, "E413.59", {"start": v(-103.4, 59.6) * mm, "end": v(-43.4, 59.28) * mm});
            skLineSegment(sketch, "E413.61", {"start": v(75.02, 100.31) * mm, "end": v(75.02, 93.91) * mm});
            skLineSegment(sketch, "E413.62", {"start": v(104.53, 94.12) * mm, "end": v(100.47, 95.16) * mm});
            skLineSegment(sketch, "E413.63", {"start": v(-32.66, 92.83) * mm, "end": v(-37.2, 92.1) * mm});
            skLineSegment(sketch, "E413.64", {"start": v(-101.14, 77.28) * mm, "end": v(-103.4, 76.7) * mm});
            skLineSegment(sketch, "E413.65", {"start": v(-23.75, 94.27) * mm, "end": v(-28.12, 93.55) * mm});
            skLineSegment(sketch, "E413.66", {"start": v(108.3, 92.8) * mm, "end": v(104.53, 94.12) * mm});
            skLineSegment(sketch, "E413.67", {"start": v(112.05, 91.25) * mm, "end": v(108.3, 92.8) * mm});
            skLineSegment(sketch, "E413.68", {"start": v(-43.4, 91.03) * mm, "end": v(-48.14, 89.92) * mm});
            skLineSegment(sketch, "E413.69", {"start": v(128.46, 81.7) * mm, "end": v(124.52, 84.4) * mm});
            skLineSegment(sketch, "E413.70", {"start": v(76.61, 100.13) * mm, "end": v(75.02, 100.31) * mm});
            skLineSegment(sketch, "E413.71", {"start": v(-19.45, 94.98) * mm, "end": v(-23.75, 94.27) * mm});
            skLineSegment(sketch, "E413.72", {"start": v(1.95, 98.25) * mm, "end": v(-2.38, 97.64) * mm});
            skLineSegment(sketch, "E413.73", {"start": v(80.98, 99.54) * mm, "end": v(76.61, 100.13) * mm});
            skLineSegment(sketch, "E413.74", {"start": v(121.05, 62.42) * mm, "end": v(124.86, 63.23) * mm});
            skLineSegment(sketch, "E413.75", {"start": v(6.36, 98.83) * mm, "end": v(1.95, 98.25) * mm});
            skLineSegment(sketch, "E413.76", {"start": v(115.72, 89.55) * mm, "end": v(112.05, 91.25) * mm});
            skLineSegment(sketch, "E413.77", {"start": v(119.34, 87.78) * mm, "end": v(115.72, 89.55) * mm});
            skLineSegment(sketch, "E413.78", {"start": v(-10.93, 96.35) * mm, "end": v(-15.18, 95.67) * mm});
            skLineSegment(sketch, "E413.79", {"start": v(134.6, 75.6) * mm, "end": v(132.03, 78.53) * mm});
            skLineSegment(sketch, "E413.81", {"start": v(130.67, 73.42) * mm, "end": v(134.6, 75.6) * mm});
            skLineSegment(sketch, "E413.82", {"start": v(90.15, 98.07) * mm, "end": v(85.63, 98.85) * mm});
            skLineSegment(sketch, "E413.83", {"start": v(-6.67, 97) * mm, "end": v(-10.93, 96.35) * mm});
            skLineSegment(sketch, "E413.84", {"start": v(131.85, 65.67) * mm, "end": v(134.32, 66.87) * mm});
            skLineSegment(sketch, "E413.85", {"start": v(15.48, 99.9) * mm, "end": v(10.86, 99.38) * mm});
            skLineSegment(sketch, "E413.86", {"start": v(128.31, 64.27) * mm, "end": v(131.85, 65.67) * mm});
            skLineSegment(sketch, "E413.87", {"start": v(124.86, 63.23) * mm, "end": v(128.31, 64.27) * mm});
            skLineSegment(sketch, "E413.88", {"start": v(116.68, 61.82) * mm, "end": v(121.05, 62.42) * mm});
            skLineSegment(sketch, "E414", {"start": v(-103.4, 59.6) * mm, "end": v(-103.4, 76.7) * mm});
            skSolve(sketch);
        }
        {
            var Q0;
            Q0=makeQuery(id+"F18.imprint","IMPRINT",FACE,{"disambiguationData":[TD([[makeQuery(id+"F18.imprint","IMPRINT",EDGE,{"derivedFrom":sQuery(id+"F18.wireOp",EDGE,"E413.1")}),1.0]])]});
            extrude(context, id + "F19", {"entities" : qUnion([Q0]), "depth" : 2 * mm});
        }
        {
            var Q0;
            Q0=qCreatedBy(makeId("Right.planeOp"),FACE);
            var sketch = newSketch(context, id + "F20", { "sketchPlane" : qUnion([Q0])});
            skLineSegment(sketch, "E415.0", {"start": v(90.15, 98.07) * mm, "end": v(85.63, 98.85) * mm});
            skLineSegment(sketch, "E415.1", {"start": v(-23.75, 94.27) * mm, "end": v(-28.12, 93.55) * mm});
            skLineSegment(sketch, "E415.2", {"start": v(-52.97, 88.81) * mm, "end": v(-57.8, 87.7) * mm});
            skLineSegment(sketch, "E415.3", {"start": v(65.82, 93.91) * mm, "end": v(65.82, 102.3) * mm});
            skLineSegment(sketch, "E415.4", {"start": v(105.7, 67.06) * mm, "end": v(105.7, 61.14) * mm});
            skLineSegment(sketch, "E415.5", {"start": v(46.82, 102) * mm, "end": v(41.06, 101.78) * mm});
            skLineSegment(sketch, "E415.6", {"start": v(121.47, 79.12) * mm, "end": v(116.13, 82.2) * mm});
            skLineSegment(sketch, "E415.7", {"start": v(65.82, 102.3) * mm, "end": v(59.19, 102.27) * mm});
            skLineSegment(sketch, "E415.8", {"start": v(-57.8, 87.7) * mm, "end": v(-62.63, 86.58) * mm});
            skLineSegment(sketch, "E415.9", {"start": v(20.23, 100.36) * mm, "end": v(15.48, 99.9) * mm});
            skLineSegment(sketch, "E415.10", {"start": v(-81.9, 82) * mm, "end": v(-86.72, 80.84) * mm});
            skCircle(sketch, "E415.11", {"center": v(-14.82, 76.96) * mm, "radius": 6.5 * mm});
            skLineSegment(sketch, "E415.12", {"start": v(134.32, 66.87) * mm, "end": v(130.67, 73.42) * mm});
            skLineSegment(sketch, "E415.13", {"start": v(10.86, 99.38) * mm, "end": v(6.36, 98.83) * mm});
            skLineSegment(sketch, "E415.14", {"start": v(75.02, 100.31) * mm, "end": v(75.02, 93.91) * mm});
            skLineSegment(sketch, "E415.15", {"start": v(-103.4, 59.6) * mm, "end": v(-43.4, 59.28) * mm});
            skLineSegment(sketch, "E415.16", {"start": v(-81.9, 82) * mm, "end": v(-72.27, 84.3) * mm});
            skLineSegment(sketch, "E415.17", {"start": v(99.85, 60.81) * mm, "end": v(99.85, 67.06) * mm});
            skLineSegment(sketch, "E415.18", {"start": v(92.83, 91.04) * mm, "end": v(94.63, 97.2) * mm});
            skLineSegment(sketch, "E415.19", {"start": v(75.02, 60.74) * mm, "end": v(99.85, 60.81) * mm});
            skLineSegment(sketch, "E415.20", {"start": v(-37.2, 59.28) * mm, "end": v(65.82, 58.98) * mm});
            skLineSegment(sketch, "E415.21", {"start": v(-43.4, 83.28) * mm, "end": v(-43.4, 91.03) * mm});
            skLineSegment(sketch, "E415.22", {"start": v(59.19, 102.27) * mm, "end": v(52.86, 102.17) * mm});
            skLineSegment(sketch, "E415.23", {"start": v(-43.4, 59.28) * mm, "end": v(-43.4, 67.28) * mm});
            skLineSegment(sketch, "E415.24", {"start": v(41.06, 101.78) * mm, "end": v(35.53, 101.5) * mm});
            skLineSegment(sketch, "E415.25", {"start": v(30.24, 101.17) * mm, "end": v(25.14, 100.8) * mm});
            skLineSegment(sketch, "E415.26", {"start": v(116.13, 82.2) * mm, "end": v(119.34, 87.78) * mm});
            skLineSegment(sketch, "E415.27", {"start": v(-37.2, 67.28) * mm, "end": v(-37.2, 59.28) * mm});
            skLineSegment(sketch, "E415.28", {"start": v(75.02, 67.11) * mm, "end": v(75.02, 60.73) * mm});
            skCircle(sketch, "E415.29", {"center": v(18.63, 79.1) * mm, "radius": 13.55 * mm});
            skLineSegment(sketch, "E415.30", {"start": v(-43.4, 67.28) * mm, "end": v(-37.2, 67.28) * mm});
            skLineSegment(sketch, "E415.31", {"start": v(105.7, 61.14) * mm, "end": v(111.6, 61.4) * mm});
            skLineSegment(sketch, "E415.32", {"start": v(-103.4, 59.6) * mm, "end": v(-103.4, 76.7) * mm});
            skLineSegment(sketch, "E415.33", {"start": v(-67.45, 85.45) * mm, "end": v(-72.27, 84.3) * mm});
            skLineSegment(sketch, "E415.34", {"start": v(99.85, 67.06) * mm, "end": v(105.7, 67.06) * mm});
            skLineSegment(sketch, "E415.35", {"start": v(124.52, 84.4) * mm, "end": v(121.47, 79.12) * mm});
            skLineSegment(sketch, "E415.36", {"start": v(98.76, 89.3) * mm, "end": v(92.83, 91.04) * mm});
            skLineSegment(sketch, "E415.37", {"start": v(65.82, 58.98) * mm, "end": v(65.82, 67.11) * mm});
            skLineSegment(sketch, "E415.38", {"start": v(75.02, 93.91) * mm, "end": v(65.82, 93.91) * mm});
            skLineSegment(sketch, "E415.39", {"start": v(-43.4, 91.03) * mm, "end": v(-48.14, 89.92) * mm});
            skLineSegment(sketch, "E415.40", {"start": v(-37.2, 83.28) * mm, "end": v(-43.4, 83.28) * mm});
            skLineSegment(sketch, "E415.41", {"start": v(65.82, 67.11) * mm, "end": v(75.02, 67.11) * mm});
            skCircle(sketch, "E415.42", {"center": v(48.53, 81.13) * mm, "radius": 6.5 * mm});
            skLineSegment(sketch, "E415.43", {"start": v(52.86, 102.17) * mm, "end": v(46.82, 102) * mm});
            skLineSegment(sketch, "E415.44", {"start": v(-91.53, 79.66) * mm, "end": v(-96.34, 78.48) * mm});
            skLineSegment(sketch, "E415.45", {"start": v(100.47, 95.16) * mm, "end": v(98.76, 89.3) * mm});
            skLineSegment(sketch, "E415.46", {"start": v(35.53, 101.5) * mm, "end": v(30.24, 101.17) * mm});
            skLineSegment(sketch, "E415.47", {"start": v(-37.2, 92.1) * mm, "end": v(-37.2, 83.28) * mm});
            skLineSegment(sketch, "E415.48", {"start": v(111.6, 61.4) * mm, "end": v(116.68, 61.82) * mm});
            skLineSegment(sketch, "E415.49", {"start": v(25.14, 100.8) * mm, "end": v(20.23, 100.36) * mm});
            skLineSegment(sketch, "E415.50", {"start": v(15.48, 99.9) * mm, "end": v(10.86, 99.38) * mm});
            skLineSegment(sketch, "E415.51", {"start": v(-86.72, 80.84) * mm, "end": v(-91.53, 79.66) * mm});
            skLineSegment(sketch, "E415.52", {"start": v(-6.67, 97) * mm, "end": v(-10.93, 96.35) * mm});
            skLineSegment(sketch, "E415.53", {"start": v(108.3, 92.8) * mm, "end": v(104.53, 94.12) * mm});
            skLineSegment(sketch, "E415.54", {"start": v(-2.38, 97.64) * mm, "end": v(-6.67, 97) * mm});
            skLineSegment(sketch, "E415.55", {"start": v(121.05, 62.42) * mm, "end": v(124.86, 63.23) * mm});
            skLineSegment(sketch, "E415.56", {"start": v(119.34, 87.78) * mm, "end": v(115.72, 89.55) * mm});
            skLineSegment(sketch, "E415.57", {"start": v(115.72, 89.55) * mm, "end": v(112.05, 91.25) * mm});
            skLineSegment(sketch, "E415.58", {"start": v(132.03, 78.53) * mm, "end": v(128.46, 81.7) * mm});
            skLineSegment(sketch, "E415.59", {"start": v(131.85, 65.67) * mm, "end": v(134.32, 66.87) * mm});
            skLineSegment(sketch, "E415.60", {"start": v(80.98, 99.54) * mm, "end": v(76.61, 100.13) * mm});
            skLineSegment(sketch, "E415.61", {"start": v(134.6, 75.6) * mm, "end": v(132.03, 78.53) * mm});
            skLineSegment(sketch, "E415.62", {"start": v(-32.66, 92.83) * mm, "end": v(-37.2, 92.1) * mm});
            skLineSegment(sketch, "E415.63", {"start": v(130.67, 73.42) * mm, "end": v(134.6, 75.6) * mm});
            skLineSegment(sketch, "E415.64", {"start": v(-101.14, 77.28) * mm, "end": v(-103.4, 76.7) * mm});
            skLineSegment(sketch, "E415.65", {"start": v(112.05, 91.25) * mm, "end": v(108.3, 92.8) * mm});
            skLineSegment(sketch, "E415.66", {"start": v(-62.63, 86.58) * mm, "end": v(-67.45, 85.45) * mm});
            skLineSegment(sketch, "E415.67", {"start": v(124.86, 63.23) * mm, "end": v(128.31, 64.27) * mm});
            skLineSegment(sketch, "E415.68", {"start": v(76.61, 100.13) * mm, "end": v(75.02, 100.31) * mm});
            skLineSegment(sketch, "E415.69", {"start": v(116.68, 61.82) * mm, "end": v(121.05, 62.42) * mm});
            skLineSegment(sketch, "E415.70", {"start": v(-19.45, 94.98) * mm, "end": v(-23.75, 94.27) * mm});
            skLineSegment(sketch, "E415.71", {"start": v(85.63, 98.85) * mm, "end": v(80.98, 99.54) * mm});
            skLineSegment(sketch, "E415.72", {"start": v(1.95, 98.25) * mm, "end": v(-2.38, 97.64) * mm});
            skLineSegment(sketch, "E415.73", {"start": v(6.36, 98.83) * mm, "end": v(1.95, 98.25) * mm});
            skLineSegment(sketch, "E415.74", {"start": v(-10.93, 96.35) * mm, "end": v(-15.18, 95.67) * mm});
            skLineSegment(sketch, "E415.75", {"start": v(104.53, 94.12) * mm, "end": v(100.47, 95.16) * mm});
            skLineSegment(sketch, "E415.76", {"start": v(128.31, 64.27) * mm, "end": v(131.85, 65.67) * mm});
            skLineSegment(sketch, "E415.77", {"start": v(128.46, 81.7) * mm, "end": v(124.52, 84.4) * mm});
            skLineSegment(sketch, "E415.78", {"start": v(-28.12, 93.55) * mm, "end": v(-32.66, 92.83) * mm});
            skLineSegment(sketch, "E415.79", {"start": v(-15.18, 95.67) * mm, "end": v(-19.45, 94.98) * mm});
            skLineSegment(sketch, "E415.80", {"start": v(-48.14, 89.92) * mm, "end": v(-52.97, 88.81) * mm});
            skLineSegment(sketch, "E415.81", {"start": v(94.63, 97.2) * mm, "end": v(90.15, 98.07) * mm});
            skLineSegment(sketch, "E415.82", {"start": v(-96.34, 78.48) * mm, "end": v(-101.14, 77.28) * mm});
            skSolve(sketch);
        }
        {
            var Q0;
            Q0 = qSketchRegion(id + "F20", true);
            var Q1;
            Q1=makeQuery(id+"F18.imprint","IMPRINT",FACE,{"disambiguationData":[TD([[makeQuery(id+"F18.imprint","IMPRINT",EDGE,{"derivedFrom":sQuery(id+"F18.wireOp",EDGE,"E413.1")}),1.0]])]});
            extrude(context, id + "F21", {"entities" : qUnion([Q0, Q1]), "depth" : 6 * mm});
        }
        {
            var Q0;
            Q0=qCreatedBy(makeId("Right.planeOp"),FACE);
            var sketch = newSketch(context, id + "F22", { "sketchPlane" : qUnion([Q0])});
            skLineSegment(sketch, "E416", {"start": v(-158.37, -1.21) * mm, "end": v(105.86, -2) * mm});
            skFitSpline(sketch, "E417", {"points": [v(-158.37, -1.21) * mm, v(-158.37, 1.04) * mm], "startDerivative": vector(-3.46, 0.12) * mm, "endDerivative": vector(2.95, 0.97) * mm});
            skFitSpline(sketch, "E418", {"points": [v(-158.37, 1.04) * mm, v(65.83, 41.5) * mm], "startDerivative": vector(227.2, 64.04) * mm, "endDerivative": vector(241.97, 0.08) * mm});
            skFitSpline(sketch, "E419", {"points": [v(65.83, 41.5) * mm, v(105.86, -2) * mm], "startDerivative": vector(184.22, 6.65) * mm, "endDerivative": vector(-197.96, 2.85) * mm});
            skSolve(sketch);
        }
        {
            var Q0;
            Q0=qCreatedBy(makeId("Top.planeOp"),FACE);
            var sketch = newSketch(context, id + "F23", { "sketchPlane" : qUnion([Q0])});
            skLineSegment(sketch, "E420", {"start": v(0, -159.17) * mm, "end": v(-0.03, 140.83) * mm});
            skFitSpline(sketch, "E421", {"points": [v(8.2, -150.2) * mm, v(-0.03, 140.83) * mm], "startDerivative": vector(41.2, 337.8) * mm, "endDerivative": vector(-86.87, 29.66) * mm});
            skFitSpline(sketch, "E422", {"points": [v(8.2, -150.2) * mm, v(0, -159.17) * mm], "startDerivative": vector(-5.2, -26.76) * mm, "endDerivative": vector(-12.36, -2.22) * mm});
            skSolve(sketch);
        }
        {
            var Q0;
            Q0 = qSketchRegion(id + "F22", true);
            extrude(context, id + "F24", {"entities" : qUnion([Q0]), "depth" : 45.37 * mm});
        }
        {
            var Q0;
            Q0=makeQuery(id+"F23.imprint","IMPRINT",FACE,{"disambiguationData":[TD([[makeQuery(id+"F23.imprint","IMPRINT",EDGE,{"derivedFrom":sQuery(id+"F23.wireOp",EDGE,"E420")}),-1.0]])]});
            var Q1;
            Q1=sQuery(id+"F23.wireOp",EDGE,"E420");
            revolve(context, id + "F25", {"operationType" : NewBodyOperationType.INTERSECT, "entities" : qUnion([Q0]), "axis" : qUnion([Q1]), "revolveType" : RevolveType.FULL});
        }
    });
